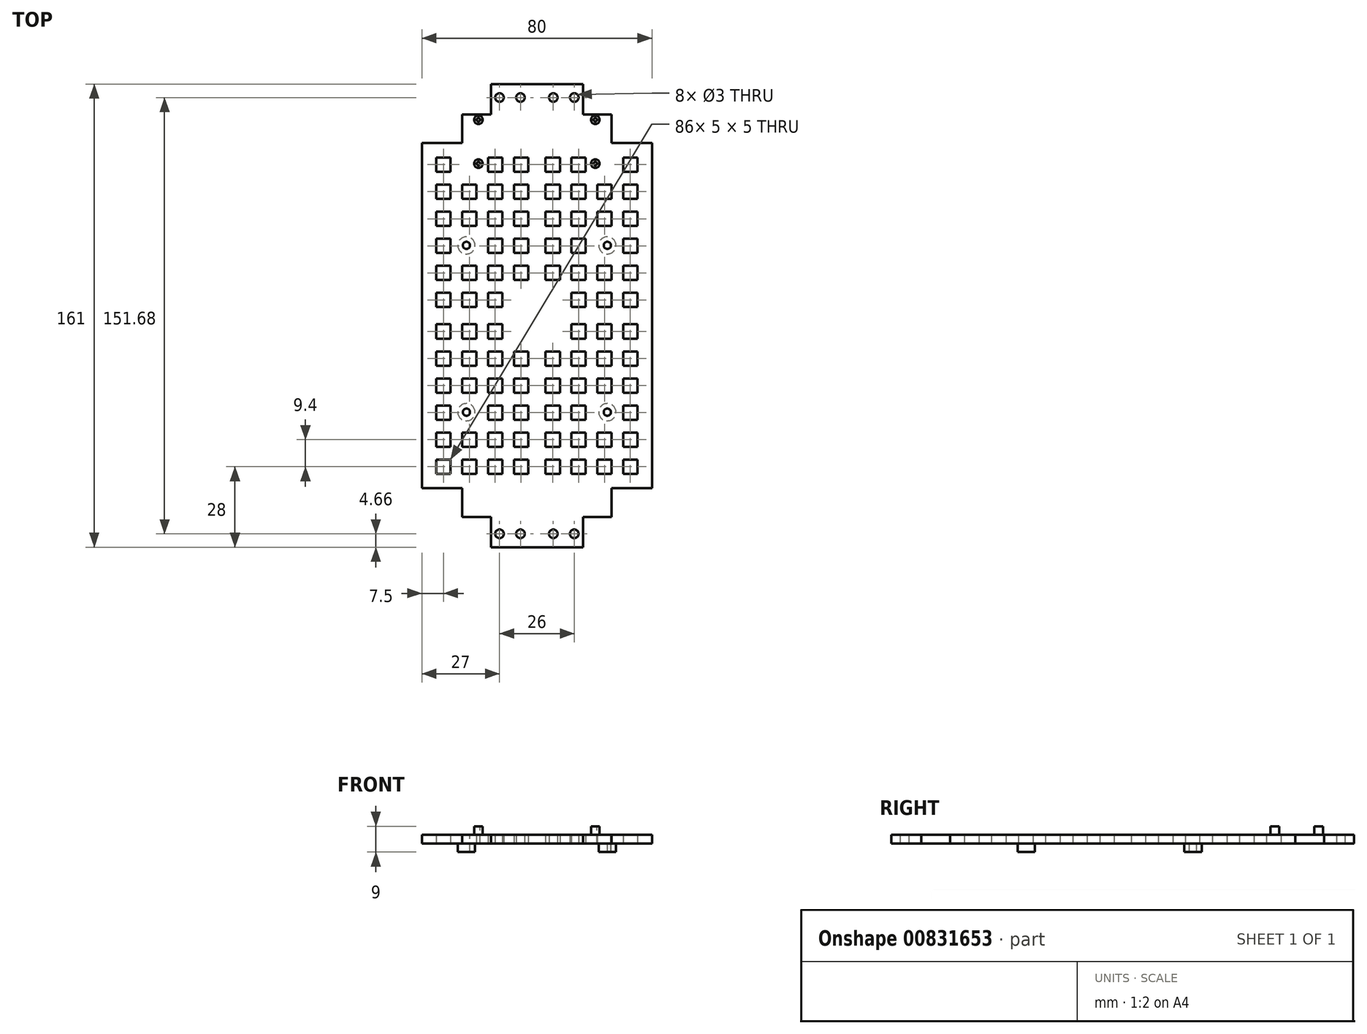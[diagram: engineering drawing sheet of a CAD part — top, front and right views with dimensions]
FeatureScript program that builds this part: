
annotation { "Feature Type Name" : "Feature", "Feature Type Description" : "" }
export const myFeature = defineFeature(function(context is Context, id is Id, definition is map)
    precondition{}
    {
        {
            var Q0;
            Q0=qCreatedBy(makeId("Top.planeOp"),FACE);
            var sketch = newSketch(context, id + "F0", { "sketchPlane" : qUnion([Q0])});
            skLineSegment(sketch, "E0", {"start": v(0, 0) * mm, "end": v(0, 77.06) * mm, "construction": true});
            skLineSegment(sketch, "E1", {"start": v(0, 0) * mm, "end": v(51.76, 0) * mm, "construction": true});
            skLineSegment(sketch, "E2", {"start": v(0, 80.5) * mm, "end": v(16, 80.5) * mm});
            skLineSegment(sketch, "E3", {"start": v(16, 80.5) * mm, "end": v(16, 70) * mm});
            skLineSegment(sketch, "E4", {"start": v(26, 60) * mm, "end": v(40, 60) * mm});
            skLineSegment(sketch, "E5", {"start": v(40, 60) * mm, "end": v(40, 0) * mm});
            skLineSegment(sketch, "E6.MirrorCS", {"start": v(-40, 60) * mm, "end": v(-40, 0) * mm});
            skLineSegment(sketch, "E7.MirrorCS", {"start": v(-26, 60) * mm, "end": v(-40, 60) * mm});
            skLineSegment(sketch, "E8.MirrorCS", {"start": v(0, 80.5) * mm, "end": v(-16, 80.5) * mm});
            skLineSegment(sketch, "E9.MirrorCS", {"start": v(40, -60) * mm, "end": v(40, 0) * mm});
            skLineSegment(sketch, "E10.MirrorCS", {"start": v(-40, -60) * mm, "end": v(-40, 0) * mm});
            skCircle(sketch, "E11", {"center": v(5.7, 75.84) * mm, "radius": 1.5 * mm});
            skCircle(sketch, "E12", {"center": v(13, 75.84) * mm, "radius": 1.5 * mm});
            skLineSegment(sketch, "E13", {"start": v(0, 75.84) * mm, "end": v(16, 75.84) * mm, "construction": true});
            skCircle(sketch, "E14.MirrorC", {"center": v(-13, 75.84) * mm, "radius": 1.5 * mm});
            skCircle(sketch, "E15.MirrorC", {"center": v(-5.7, 75.84) * mm, "radius": 1.5 * mm});
            skLineSegment(sketch, "E16", {"start": v(16, 70) * mm, "end": v(26, 70) * mm});
            skLineSegment(sketch, "E17", {"start": v(26, 70) * mm, "end": v(26, 60) * mm});
            skLineSegment(sketch, "E18.MirrorCS", {"start": v(-26, 70) * mm, "end": v(-26, 60) * mm});
            skLineSegment(sketch, "E19.MirrorCS", {"start": v(-16, 80.5) * mm, "end": v(-16, 70) * mm});
            skLineSegment(sketch, "E20.MirrorCS", {"start": v(-16, 70) * mm, "end": v(-26, 70) * mm});
            skLineSegment(sketch, "E21.MirrorCS", {"start": v(-26, -60) * mm, "end": v(-40, -60) * mm});
            skLineSegment(sketch, "E22.MirrorCS", {"start": v(26, -60) * mm, "end": v(40, -60) * mm});
            skLineSegment(sketch, "E23.MirrorCS", {"start": v(26, -70) * mm, "end": v(26, -60) * mm});
            skLineSegment(sketch, "E24.MirrorCS", {"start": v(16, -70) * mm, "end": v(26, -70) * mm});
            skLineSegment(sketch, "E25.MirrorCS", {"start": v(16, -80.5) * mm, "end": v(16, -70) * mm});
            skLineSegment(sketch, "E26.MirrorCS", {"start": v(0, -80.5) * mm, "end": v(16, -80.5) * mm});
            skLineSegment(sketch, "E27.MirrorCS", {"start": v(0, -80.5) * mm, "end": v(-16, -80.5) * mm});
            skLineSegment(sketch, "E28.MirrorCS", {"start": v(-16, -80.5) * mm, "end": v(-16, -70) * mm});
            skLineSegment(sketch, "E29.MirrorCS", {"start": v(-26, -70) * mm, "end": v(-26, -60) * mm});
            skLineSegment(sketch, "E30.MirrorCS", {"start": v(-16, -70) * mm, "end": v(-26, -70) * mm});
            skCircle(sketch, "E31.MirrorC", {"center": v(13, -75.84) * mm, "radius": 1.5 * mm});
            skCircle(sketch, "E32.MirrorC", {"center": v(5.7, -75.84) * mm, "radius": 1.5 * mm});
            skCircle(sketch, "E33.MirrorC", {"center": v(-13, -75.84) * mm, "radius": 1.5 * mm});
            skCircle(sketch, "E34.MirrorC", {"center": v(-5.7, -75.84) * mm, "radius": 1.5 * mm});
            skLineSegment(sketch, "E35.bottom", {"start": v(35, 50) * mm, "end": v(30, 50) * mm});
            skLineSegment(sketch, "E35.top", {"start": v(35, 55) * mm, "end": v(30, 55) * mm});
            skLineSegment(sketch, "E35.left", {"start": v(35, 50) * mm, "end": v(35, 55) * mm});
            skLineSegment(sketch, "E35.right", {"start": v(30, 50) * mm, "end": v(30, 55) * mm});
            skPoint(sketch, "E35.middle", {"position": v(32.5, 52.5) * mm});
            skPoint(sketch, "E36.1.0.0", {"position": v(23.5, 52.5) * mm});
            skLineSegment(sketch, "E36.1.0.1", {"start": v(26, 55) * mm, "end": v(21, 55) * mm, "construction": true});
            skLineSegment(sketch, "E36.1.0.2", {"start": v(26, 50) * mm, "end": v(21, 50) * mm});
            skLineSegment(sketch, "E36.1.0.3", {"start": v(21, 50) * mm, "end": v(21, 55) * mm, "construction": true});
            skLineSegment(sketch, "E36.1.0.4", {"start": v(26, 50) * mm, "end": v(26, 55) * mm, "construction": true});
            skPoint(sketch, "E36.2.0.0", {"position": v(14.5, 52.5) * mm});
            skLineSegment(sketch, "E36.2.0.1", {"start": v(17, 55) * mm, "end": v(12, 55) * mm});
            skLineSegment(sketch, "E36.2.0.2", {"start": v(17, 50) * mm, "end": v(12, 50) * mm});
            skLineSegment(sketch, "E36.2.0.3", {"start": v(12, 50) * mm, "end": v(12, 55) * mm});
            skLineSegment(sketch, "E36.2.0.4", {"start": v(17, 50) * mm, "end": v(17, 55) * mm});
            skLineSegment(sketch, "E36.direction1", {"start": v(30, 50) * mm, "end": v(21, 50) * mm, "construction": true});
            skPoint(sketch, "E37.0.3.0", {"position": v(5.5, 52.5) * mm});
            skLineSegment(sketch, "E37.1.3.0", {"start": v(8, 55) * mm, "end": v(3, 55) * mm});
            skLineSegment(sketch, "E37.4.3.0", {"start": v(8, 50) * mm, "end": v(3, 50) * mm});
            skLineSegment(sketch, "E37.7.3.0", {"start": v(3, 50) * mm, "end": v(3, 55) * mm});
            skLineSegment(sketch, "E37.10.3.0", {"start": v(8, 50) * mm, "end": v(8, 55) * mm});
            skLineSegment(sketch, "E38.1.0.0", {"start": v(17, 40.6) * mm, "end": v(17, 45.6) * mm});
            skLineSegment(sketch, "E38.1.0.1", {"start": v(3, 40.6) * mm, "end": v(3, 45.6) * mm});
            skLineSegment(sketch, "E38.1.0.2", {"start": v(21, 40.6) * mm, "end": v(21, 45.6) * mm});
            skPoint(sketch, "E38.1.0.3", {"position": v(5.5, 43.1) * mm});
            skLineSegment(sketch, "E38.1.0.4", {"start": v(26, 40.6) * mm, "end": v(26, 45.6) * mm});
            skLineSegment(sketch, "E38.1.0.5", {"start": v(30, 40.6) * mm, "end": v(21, 40.6) * mm, "construction": true});
            skLineSegment(sketch, "E38.1.0.6", {"start": v(35, 45.6) * mm, "end": v(30, 45.6) * mm});
            skLineSegment(sketch, "E38.1.0.7", {"start": v(35, 40.6) * mm, "end": v(35, 45.6) * mm});
            skLineSegment(sketch, "E38.1.0.8", {"start": v(12, 40.6) * mm, "end": v(12, 45.6) * mm});
            skLineSegment(sketch, "E38.1.0.9", {"start": v(17, 40.6) * mm, "end": v(12, 40.6) * mm});
            skPoint(sketch, "E38.1.0.10", {"position": v(23.5, 43.1) * mm});
            skLineSegment(sketch, "E38.1.0.11", {"start": v(8, 40.6) * mm, "end": v(8, 45.6) * mm});
            skLineSegment(sketch, "E38.1.0.12", {"start": v(26, 45.6) * mm, "end": v(21, 45.6) * mm});
            skLineSegment(sketch, "E38.1.0.13", {"start": v(17, 45.6) * mm, "end": v(12, 45.6) * mm});
            skPoint(sketch, "E38.1.0.14", {"position": v(14.5, 43.1) * mm});
            skLineSegment(sketch, "E38.1.0.15", {"start": v(8, 40.6) * mm, "end": v(3, 40.6) * mm});
            skLineSegment(sketch, "E38.1.0.16", {"start": v(35, 40.6) * mm, "end": v(30, 40.6) * mm});
            skPoint(sketch, "E38.1.0.17", {"position": v(32.5, 43.1) * mm});
            skLineSegment(sketch, "E38.1.0.18", {"start": v(8, 45.6) * mm, "end": v(3, 45.6) * mm});
            skLineSegment(sketch, "E38.1.0.19", {"start": v(30, 40.6) * mm, "end": v(30, 45.6) * mm});
            skLineSegment(sketch, "E38.1.0.20", {"start": v(26, 40.6) * mm, "end": v(21, 40.6) * mm});
            skLineSegment(sketch, "E38.2.0.0", {"start": v(17, 31.2) * mm, "end": v(17, 36.2) * mm});
            skLineSegment(sketch, "E38.2.0.1", {"start": v(3, 31.2) * mm, "end": v(3, 36.2) * mm});
            skLineSegment(sketch, "E38.2.0.2", {"start": v(21, 31.2) * mm, "end": v(21, 36.2) * mm});
            skPoint(sketch, "E38.2.0.3", {"position": v(5.5, 33.7) * mm});
            skLineSegment(sketch, "E38.2.0.4", {"start": v(26, 31.2) * mm, "end": v(26, 36.2) * mm});
            skLineSegment(sketch, "E38.2.0.5", {"start": v(30, 31.2) * mm, "end": v(21, 31.2) * mm, "construction": true});
            skLineSegment(sketch, "E38.2.0.6", {"start": v(35, 36.2) * mm, "end": v(30, 36.2) * mm});
            skLineSegment(sketch, "E38.2.0.7", {"start": v(35, 31.2) * mm, "end": v(35, 36.2) * mm});
            skLineSegment(sketch, "E38.2.0.8", {"start": v(12, 31.2) * mm, "end": v(12, 36.2) * mm});
            skLineSegment(sketch, "E38.2.0.9", {"start": v(17, 31.2) * mm, "end": v(12, 31.2) * mm});
            skPoint(sketch, "E38.2.0.10", {"position": v(23.5, 33.7) * mm});
            skLineSegment(sketch, "E38.2.0.11", {"start": v(8, 31.2) * mm, "end": v(8, 36.2) * mm});
            skLineSegment(sketch, "E38.2.0.12", {"start": v(26, 36.2) * mm, "end": v(21, 36.2) * mm});
            skLineSegment(sketch, "E38.2.0.13", {"start": v(17, 36.2) * mm, "end": v(12, 36.2) * mm});
            skPoint(sketch, "E38.2.0.14", {"position": v(14.5, 33.7) * mm});
            skLineSegment(sketch, "E38.2.0.15", {"start": v(8, 31.2) * mm, "end": v(3, 31.2) * mm});
            skLineSegment(sketch, "E38.2.0.16", {"start": v(35, 31.2) * mm, "end": v(30, 31.2) * mm});
            skPoint(sketch, "E38.2.0.17", {"position": v(32.5, 33.7) * mm});
            skLineSegment(sketch, "E38.2.0.18", {"start": v(8, 36.2) * mm, "end": v(3, 36.2) * mm});
            skLineSegment(sketch, "E38.2.0.19", {"start": v(30, 31.2) * mm, "end": v(30, 36.2) * mm});
            skLineSegment(sketch, "E38.2.0.20", {"start": v(26, 31.2) * mm, "end": v(21, 31.2) * mm});
            skLineSegment(sketch, "E38.direction1", {"start": v(3, 50) * mm, "end": v(3, 40.6) * mm, "construction": true});
            skLineSegment(sketch, "E39.0.3.0", {"start": v(17, 21.8) * mm, "end": v(17, 26.8) * mm});
            skLineSegment(sketch, "E39.3.3.0", {"start": v(3, 21.8) * mm, "end": v(3, 26.8) * mm});
            skLineSegment(sketch, "E39.6.3.0", {"start": v(21, 21.8) * mm, "end": v(21, 26.8) * mm, "construction": true});
            skPoint(sketch, "E39.9.3.0", {"position": v(5.5, 24.3) * mm});
            skLineSegment(sketch, "E39.10.3.0", {"start": v(26, 21.8) * mm, "end": v(26, 26.8) * mm, "construction": true});
            skLineSegment(sketch, "E39.13.3.0", {"start": v(30, 21.8) * mm, "end": v(21, 21.8) * mm, "construction": true});
            skLineSegment(sketch, "E39.16.3.0", {"start": v(35, 26.8) * mm, "end": v(30, 26.8) * mm});
            skLineSegment(sketch, "E39.19.3.0", {"start": v(35, 21.8) * mm, "end": v(35, 26.8) * mm});
            skLineSegment(sketch, "E39.22.3.0", {"start": v(12, 21.8) * mm, "end": v(12, 26.8) * mm});
            skLineSegment(sketch, "E39.25.3.0", {"start": v(17, 21.8) * mm, "end": v(12, 21.8) * mm});
            skPoint(sketch, "E39.28.3.0", {"position": v(23.5, 24.3) * mm});
            skLineSegment(sketch, "E39.29.3.0", {"start": v(8, 21.8) * mm, "end": v(8, 26.8) * mm});
            skLineSegment(sketch, "E39.32.3.0", {"start": v(26, 26.8) * mm, "end": v(21, 26.8) * mm, "construction": true});
            skLineSegment(sketch, "E39.35.3.0", {"start": v(17, 26.8) * mm, "end": v(12, 26.8) * mm});
            skPoint(sketch, "E39.38.3.0", {"position": v(14.5, 24.3) * mm});
            skLineSegment(sketch, "E39.39.3.0", {"start": v(8, 21.8) * mm, "end": v(3, 21.8) * mm});
            skLineSegment(sketch, "E39.42.3.0", {"start": v(35, 21.8) * mm, "end": v(30, 21.8) * mm});
            skPoint(sketch, "E39.45.3.0", {"position": v(32.5, 24.3) * mm});
            skLineSegment(sketch, "E39.46.3.0", {"start": v(8, 26.8) * mm, "end": v(3, 26.8) * mm});
            skLineSegment(sketch, "E39.49.3.0", {"start": v(30, 21.8) * mm, "end": v(30, 26.8) * mm});
            skLineSegment(sketch, "E39.52.3.0", {"start": v(26, 21.8) * mm, "end": v(21, 21.8) * mm, "construction": true});
            skLineSegment(sketch, "E39.0.4.0", {"start": v(17, 12.4) * mm, "end": v(17, 17.4) * mm});
            skLineSegment(sketch, "E39.3.4.0", {"start": v(3, 12.4) * mm, "end": v(3, 17.4) * mm});
            skLineSegment(sketch, "E39.6.4.0", {"start": v(21, 12.4) * mm, "end": v(21, 17.4) * mm});
            skPoint(sketch, "E39.9.4.0", {"position": v(5.5, 14.9) * mm});
            skLineSegment(sketch, "E39.10.4.0", {"start": v(26, 12.4) * mm, "end": v(26, 17.4) * mm});
            skLineSegment(sketch, "E39.13.4.0", {"start": v(30, 12.4) * mm, "end": v(21, 12.4) * mm, "construction": true});
            skLineSegment(sketch, "E39.16.4.0", {"start": v(35, 17.4) * mm, "end": v(30, 17.4) * mm});
            skLineSegment(sketch, "E39.19.4.0", {"start": v(35, 12.4) * mm, "end": v(35, 17.4) * mm});
            skLineSegment(sketch, "E39.22.4.0", {"start": v(12, 12.4) * mm, "end": v(12, 17.4) * mm});
            skLineSegment(sketch, "E39.25.4.0", {"start": v(17, 12.4) * mm, "end": v(12, 12.4) * mm});
            skPoint(sketch, "E39.28.4.0", {"position": v(23.5, 14.9) * mm});
            skLineSegment(sketch, "E39.29.4.0", {"start": v(8, 12.4) * mm, "end": v(8, 17.4) * mm});
            skLineSegment(sketch, "E39.32.4.0", {"start": v(26, 17.4) * mm, "end": v(21, 17.4) * mm});
            skLineSegment(sketch, "E39.35.4.0", {"start": v(17, 17.4) * mm, "end": v(12, 17.4) * mm});
            skPoint(sketch, "E39.38.4.0", {"position": v(14.5, 14.9) * mm});
            skLineSegment(sketch, "E39.39.4.0", {"start": v(8, 12.4) * mm, "end": v(3, 12.4) * mm});
            skLineSegment(sketch, "E39.42.4.0", {"start": v(35, 12.4) * mm, "end": v(30, 12.4) * mm});
            skPoint(sketch, "E39.45.4.0", {"position": v(32.5, 14.9) * mm});
            skLineSegment(sketch, "E39.46.4.0", {"start": v(8, 17.4) * mm, "end": v(3, 17.4) * mm});
            skLineSegment(sketch, "E39.49.4.0", {"start": v(30, 12.4) * mm, "end": v(30, 17.4) * mm});
            skLineSegment(sketch, "E39.52.4.0", {"start": v(26, 12.4) * mm, "end": v(21, 12.4) * mm});
            skLineSegment(sketch, "E39.0.5.0", {"start": v(17, 3) * mm, "end": v(17, 8) * mm});
            skLineSegment(sketch, "E39.3.5.0", {"start": v(3, 3) * mm, "end": v(3, 8) * mm, "construction": true});
            skLineSegment(sketch, "E39.6.5.0", {"start": v(21, 3) * mm, "end": v(21, 8) * mm});
            skPoint(sketch, "E39.9.5.0", {"position": v(5.5, 5.5) * mm});
            skLineSegment(sketch, "E39.10.5.0", {"start": v(26, 3) * mm, "end": v(26, 8) * mm});
            skLineSegment(sketch, "E39.13.5.0", {"start": v(30, 3) * mm, "end": v(21, 3) * mm, "construction": true});
            skLineSegment(sketch, "E39.16.5.0", {"start": v(35, 8) * mm, "end": v(30, 8) * mm});
            skLineSegment(sketch, "E39.19.5.0", {"start": v(35, 3) * mm, "end": v(35, 8) * mm});
            skLineSegment(sketch, "E39.22.5.0", {"start": v(12, 3) * mm, "end": v(12, 8) * mm});
            skLineSegment(sketch, "E39.25.5.0", {"start": v(17, 3) * mm, "end": v(12, 3) * mm});
            skPoint(sketch, "E39.28.5.0", {"position": v(23.5, 5.5) * mm});
            skLineSegment(sketch, "E39.29.5.0", {"start": v(8, 3) * mm, "end": v(8, 8) * mm, "construction": true});
            skLineSegment(sketch, "E39.32.5.0", {"start": v(26, 8) * mm, "end": v(21, 8) * mm});
            skLineSegment(sketch, "E39.35.5.0", {"start": v(17, 8) * mm, "end": v(12, 8) * mm});
            skPoint(sketch, "E39.38.5.0", {"position": v(14.5, 5.5) * mm});
            skLineSegment(sketch, "E39.39.5.0", {"start": v(8, 3) * mm, "end": v(3, 3) * mm, "construction": true});
            skLineSegment(sketch, "E39.42.5.0", {"start": v(35, 3) * mm, "end": v(30, 3) * mm});
            skPoint(sketch, "E39.45.5.0", {"position": v(32.5, 5.5) * mm});
            skLineSegment(sketch, "E39.46.5.0", {"start": v(8, 8) * mm, "end": v(3, 8) * mm, "construction": true});
            skLineSegment(sketch, "E39.49.5.0", {"start": v(30, 3) * mm, "end": v(30, 8) * mm});
            skLineSegment(sketch, "E39.52.5.0", {"start": v(26, 3) * mm, "end": v(21, 3) * mm});
            skLineSegment(sketch, "E40.MirrorCS", {"start": v(-26, 3) * mm, "end": v(-21, 3) * mm});
            skLineSegment(sketch, "E41.MirrorCS", {"start": v(-35, 45.6) * mm, "end": v(-30, 45.6) * mm});
            skLineSegment(sketch, "E42.MirrorCS", {"start": v(-26, 12.4) * mm, "end": v(-21, 12.4) * mm});
            skLineSegment(sketch, "E43.MirrorCS", {"start": v(-26, 50) * mm, "end": v(-21, 50) * mm});
            skLineSegment(sketch, "E44.MirrorCS", {"start": v(-26, 21.8) * mm, "end": v(-21, 21.8) * mm, "construction": true});
            skLineSegment(sketch, "E45.MirrorCS", {"start": v(-3, 40.6) * mm, "end": v(-3, 45.6) * mm});
            skLineSegment(sketch, "E46.MirrorCS", {"start": v(-26, 31.2) * mm, "end": v(-21, 31.2) * mm});
            skLineSegment(sketch, "E47.MirrorCS", {"start": v(-26, 40.6) * mm, "end": v(-21, 40.6) * mm});
            skPoint(sketch, "E48.MirrorP", {"position": v(-14.5, 52.5) * mm});
            skPoint(sketch, "E49.MirrorP", {"position": v(-14.5, 14.9) * mm});
            skLineSegment(sketch, "E50.MirrorCS", {"start": v(-30, 3) * mm, "end": v(-21, 3) * mm, "construction": true});
            skLineSegment(sketch, "E51.MirrorCS", {"start": v(-35, 17.4) * mm, "end": v(-30, 17.4) * mm});
            skLineSegment(sketch, "E52.MirrorCS", {"start": v(-8, 40.6) * mm, "end": v(-8, 45.6) * mm});
            skLineSegment(sketch, "E53.MirrorCS", {"start": v(-12, 50) * mm, "end": v(-12, 55) * mm});
            skPoint(sketch, "E54.MirrorP", {"position": v(-23.5, 52.5) * mm});
            skLineSegment(sketch, "E55.MirrorCS", {"start": v(-17, 31.2) * mm, "end": v(-12, 31.2) * mm});
            skPoint(sketch, "E56.MirrorP", {"position": v(-23.5, 14.9) * mm});
            skLineSegment(sketch, "E57.MirrorCS", {"start": v(-35, 21.8) * mm, "end": v(-35, 26.8) * mm});
            skLineSegment(sketch, "E58.MirrorCS", {"start": v(-26, 8) * mm, "end": v(-21, 8) * mm});
            skLineSegment(sketch, "E59.MirrorCS", {"start": v(-8, 36.2) * mm, "end": v(-3, 36.2) * mm});
            skLineSegment(sketch, "E60.MirrorCS", {"start": v(-30, 40.6) * mm, "end": v(-30, 45.6) * mm});
            skPoint(sketch, "E61.MirrorP", {"position": v(-32.5, 43.1) * mm});
            skLineSegment(sketch, "E62.MirrorCS", {"start": v(-17, 17.4) * mm, "end": v(-12, 17.4) * mm});
            skLineSegment(sketch, "E63.MirrorCS", {"start": v(-35, 50) * mm, "end": v(-30, 50) * mm});
            skLineSegment(sketch, "E64.MirrorCS", {"start": v(-8, 50) * mm, "end": v(-8, 55) * mm});
            skPoint(sketch, "E65.MirrorP", {"position": v(-32.5, 5.5) * mm});
            skLineSegment(sketch, "E66.MirrorCS", {"start": v(-17, 26.8) * mm, "end": v(-12, 26.8) * mm});
            skLineSegment(sketch, "E67.MirrorCS", {"start": v(-8, 45.6) * mm, "end": v(-3, 45.6) * mm});
            skLineSegment(sketch, "E68.MirrorCS", {"start": v(-3, 50) * mm, "end": v(-3, 55) * mm});
            skLineSegment(sketch, "E69.MirrorCS", {"start": v(-8, 3) * mm, "end": v(-8, 8) * mm, "construction": true});
            skPoint(sketch, "E70.MirrorP", {"position": v(-14.5, 5.5) * mm});
            skPoint(sketch, "E71.MirrorP", {"position": v(-14.5, 43.1) * mm});
            skLineSegment(sketch, "E72.MirrorCS", {"start": v(-35, 31.2) * mm, "end": v(-30, 31.2) * mm});
            skLineSegment(sketch, "E73.MirrorCS", {"start": v(-26, 17.4) * mm, "end": v(-21, 17.4) * mm});
            skLineSegment(sketch, "E74.MirrorCS", {"start": v(-17, 3) * mm, "end": v(-12, 3) * mm});
            skLineSegment(sketch, "E75.MirrorCS", {"start": v(-26, 26.8) * mm, "end": v(-21, 26.8) * mm, "construction": true});
            skLineSegment(sketch, "E76.MirrorCS", {"start": v(-8, 12.4) * mm, "end": v(-8, 17.4) * mm});
            skLineSegment(sketch, "E77.MirrorCS", {"start": v(-35, 40.6) * mm, "end": v(-30, 40.6) * mm});
            skLineSegment(sketch, "E78.MirrorCS", {"start": v(-8, 50) * mm, "end": v(-3, 50) * mm});
            skLineSegment(sketch, "E79.MirrorCS", {"start": v(-8, 31.2) * mm, "end": v(-3, 31.2) * mm});
            skPoint(sketch, "E80.MirrorP", {"position": v(-23.5, 43.1) * mm});
            skPoint(sketch, "E81.MirrorP", {"position": v(-23.5, 5.5) * mm});
            skLineSegment(sketch, "E82.MirrorCS", {"start": v(-30, 12.4) * mm, "end": v(-21, 12.4) * mm, "construction": true});
            skLineSegment(sketch, "E83.MirrorCS", {"start": v(-35, 26.8) * mm, "end": v(-30, 26.8) * mm});
            skLineSegment(sketch, "E84.MirrorCS", {"start": v(-17, 40.6) * mm, "end": v(-12, 40.6) * mm});
            skLineSegment(sketch, "E85.MirrorCS", {"start": v(-12, 31.2) * mm, "end": v(-12, 36.2) * mm});
            skLineSegment(sketch, "E86.MirrorCS", {"start": v(-26, 3) * mm, "end": v(-26, 8) * mm});
            skLineSegment(sketch, "E87.MirrorCS", {"start": v(-17, 50) * mm, "end": v(-12, 50) * mm});
            skPoint(sketch, "E88.MirrorP", {"position": v(-5.5, 14.9) * mm});
            skPoint(sketch, "E89.MirrorP", {"position": v(-32.5, 52.5) * mm});
            skPoint(sketch, "E90.MirrorP", {"position": v(-32.5, 24.3) * mm});
            skPoint(sketch, "E91.MirrorP", {"position": v(-14.5, 24.3) * mm});
            skLineSegment(sketch, "E92.MirrorCS", {"start": v(-35, 31.2) * mm, "end": v(-35, 36.2) * mm});
            skLineSegment(sketch, "E93.MirrorCS", {"start": v(-26, 12.4) * mm, "end": v(-26, 17.4) * mm});
            skLineSegment(sketch, "E94.MirrorCS", {"start": v(-30, 21.8) * mm, "end": v(-21, 21.8) * mm, "construction": true});
            skLineSegment(sketch, "E95.MirrorCS", {"start": v(-17, 55) * mm, "end": v(-12, 55) * mm});
            skLineSegment(sketch, "E96.MirrorCS", {"start": v(-21, 3) * mm, "end": v(-21, 8) * mm});
            skLineSegment(sketch, "E97.MirrorCS", {"start": v(-3, 3) * mm, "end": v(-3, 8) * mm, "construction": true});
            skLineSegment(sketch, "E98.MirrorCS", {"start": v(-35, 36.2) * mm, "end": v(-30, 36.2) * mm});
            skLineSegment(sketch, "E99.MirrorCS", {"start": v(-35, 40.6) * mm, "end": v(-35, 45.6) * mm});
            skLineSegment(sketch, "E100.MirrorCS", {"start": v(-26, 50) * mm, "end": v(-26, 55) * mm, "construction": true});
            skLineSegment(sketch, "E101.MirrorCS", {"start": v(-12, 40.6) * mm, "end": v(-12, 45.6) * mm});
            skLineSegment(sketch, "E102.MirrorCS", {"start": v(-26, 21.8) * mm, "end": v(-26, 26.8) * mm, "construction": true});
            skLineSegment(sketch, "E103.MirrorCS", {"start": v(-21, 12.4) * mm, "end": v(-21, 17.4) * mm});
            skLineSegment(sketch, "E104.MirrorCS", {"start": v(-8, 55) * mm, "end": v(-3, 55) * mm});
            skLineSegment(sketch, "E105.MirrorCS", {"start": v(-30, 31.2) * mm, "end": v(-21, 31.2) * mm, "construction": true});
            skLineSegment(sketch, "E106.MirrorCS", {"start": v(-17, 3) * mm, "end": v(-17, 8) * mm});
            skLineSegment(sketch, "E107.MirrorCS", {"start": v(-3, 12.4) * mm, "end": v(-3, 17.4) * mm});
            skLineSegment(sketch, "E108.MirrorCS", {"start": v(-21, 21.8) * mm, "end": v(-21, 26.8) * mm, "construction": true});
            skLineSegment(sketch, "E109.MirrorCS", {"start": v(-8, 40.6) * mm, "end": v(-3, 40.6) * mm});
            skPoint(sketch, "E110.MirrorP", {"position": v(-5.5, 5.5) * mm});
            skPoint(sketch, "E111.MirrorP", {"position": v(-5.5, 43.1) * mm});
            skLineSegment(sketch, "E112.MirrorCS", {"start": v(-17, 36.2) * mm, "end": v(-12, 36.2) * mm});
            skLineSegment(sketch, "E113.MirrorCS", {"start": v(-21, 50) * mm, "end": v(-21, 55) * mm, "construction": true});
            skPoint(sketch, "E114.MirrorP", {"position": v(-23.5, 24.3) * mm});
            skPoint(sketch, "E115.MirrorP", {"position": v(-5.5, 24.3) * mm});
            skLineSegment(sketch, "E116.MirrorCS", {"start": v(-17, 12.4) * mm, "end": v(-12, 12.4) * mm});
            skLineSegment(sketch, "E117.MirrorCS", {"start": v(-8, 21.8) * mm, "end": v(-8, 26.8) * mm});
            skLineSegment(sketch, "E118.MirrorCS", {"start": v(-30, 40.6) * mm, "end": v(-21, 40.6) * mm, "construction": true});
            skLineSegment(sketch, "E119.MirrorCS", {"start": v(-30, 3) * mm, "end": v(-30, 8) * mm});
            skLineSegment(sketch, "E120.MirrorCS", {"start": v(-17, 12.4) * mm, "end": v(-17, 17.4) * mm});
            skLineSegment(sketch, "E121.MirrorCS", {"start": v(-26, 31.2) * mm, "end": v(-26, 36.2) * mm});
            skLineSegment(sketch, "E122.MirrorCS", {"start": v(-26, 55) * mm, "end": v(-21, 55) * mm, "construction": true});
            skLineSegment(sketch, "E123.MirrorCS", {"start": v(-3, 21.8) * mm, "end": v(-3, 26.8) * mm});
            skLineSegment(sketch, "E124.MirrorCS", {"start": v(-8, 8) * mm, "end": v(-3, 8) * mm, "construction": true});
            skLineSegment(sketch, "E125.MirrorCS", {"start": v(-12, 3) * mm, "end": v(-12, 8) * mm});
            skLineSegment(sketch, "E126.MirrorCS", {"start": v(-30, 12.4) * mm, "end": v(-30, 17.4) * mm});
            skLineSegment(sketch, "E127.MirrorCS", {"start": v(-17, 21.8) * mm, "end": v(-17, 26.8) * mm});
            skLineSegment(sketch, "E128.MirrorCS", {"start": v(-8, 17.4) * mm, "end": v(-3, 17.4) * mm});
            skLineSegment(sketch, "E129.MirrorCS", {"start": v(-30, 50) * mm, "end": v(-21, 50) * mm, "construction": true});
            skLineSegment(sketch, "E130.MirrorCS", {"start": v(-3, 50) * mm, "end": v(-3, 40.6) * mm, "construction": true});
            skLineSegment(sketch, "E131.MirrorCS", {"start": v(-21, 40.6) * mm, "end": v(-21, 45.6) * mm});
            skLineSegment(sketch, "E132.MirrorCS", {"start": v(-30, 50) * mm, "end": v(-30, 55) * mm});
            skLineSegment(sketch, "E133.MirrorCS", {"start": v(-21, 31.2) * mm, "end": v(-21, 36.2) * mm});
            skLineSegment(sketch, "E134.MirrorCS", {"start": v(-30, 21.8) * mm, "end": v(-30, 26.8) * mm});
            skLineSegment(sketch, "E135.MirrorCS", {"start": v(-3, 31.2) * mm, "end": v(-3, 36.2) * mm});
            skLineSegment(sketch, "E136.MirrorCS", {"start": v(-35, 3) * mm, "end": v(-30, 3) * mm});
            skLineSegment(sketch, "E137.MirrorCS", {"start": v(-26, 40.6) * mm, "end": v(-26, 45.6) * mm});
            skPoint(sketch, "E138.MirrorP", {"position": v(-32.5, 33.7) * mm});
            skLineSegment(sketch, "E139.MirrorCS", {"start": v(-35, 3) * mm, "end": v(-35, 8) * mm});
            skLineSegment(sketch, "E140.MirrorCS", {"start": v(-12, 12.4) * mm, "end": v(-12, 17.4) * mm});
            skLineSegment(sketch, "E141.MirrorCS", {"start": v(-17, 21.8) * mm, "end": v(-12, 21.8) * mm});
            skPoint(sketch, "E142.MirrorP", {"position": v(-14.5, 33.7) * mm});
            skLineSegment(sketch, "E143.MirrorCS", {"start": v(-8, 3) * mm, "end": v(-3, 3) * mm, "construction": true});
            skLineSegment(sketch, "E144.MirrorCS", {"start": v(-17, 31.2) * mm, "end": v(-17, 36.2) * mm});
            skLineSegment(sketch, "E145.MirrorCS", {"start": v(-35, 12.4) * mm, "end": v(-30, 12.4) * mm});
            skLineSegment(sketch, "E146.MirrorCS", {"start": v(-35, 50) * mm, "end": v(-35, 55) * mm});
            skLineSegment(sketch, "E147.MirrorCS", {"start": v(-8, 26.8) * mm, "end": v(-3, 26.8) * mm});
            skLineSegment(sketch, "E148.MirrorCS", {"start": v(-17, 45.6) * mm, "end": v(-12, 45.6) * mm});
            skLineSegment(sketch, "E149.MirrorCS", {"start": v(-26, 36.2) * mm, "end": v(-21, 36.2) * mm});
            skLineSegment(sketch, "E150.MirrorCS", {"start": v(-8, 21.8) * mm, "end": v(-3, 21.8) * mm});
            skPoint(sketch, "E151.MirrorP", {"position": v(-5.5, 52.5) * mm});
            skPoint(sketch, "E152.MirrorP", {"position": v(-32.5, 14.9) * mm});
            skPoint(sketch, "E153.MirrorP", {"position": v(-23.5, 33.7) * mm});
            skLineSegment(sketch, "E154.MirrorCS", {"start": v(-17, 8) * mm, "end": v(-12, 8) * mm});
            skLineSegment(sketch, "E155.MirrorCS", {"start": v(-17, 40.6) * mm, "end": v(-17, 45.6) * mm});
            skLineSegment(sketch, "E156.MirrorCS", {"start": v(-35, 55) * mm, "end": v(-30, 55) * mm});
            skPoint(sketch, "E157.MirrorP", {"position": v(-5.5, 33.7) * mm});
            skLineSegment(sketch, "E158.MirrorCS", {"start": v(-8, 12.4) * mm, "end": v(-3, 12.4) * mm});
            skLineSegment(sketch, "E159.MirrorCS", {"start": v(-35, 21.8) * mm, "end": v(-30, 21.8) * mm});
            skLineSegment(sketch, "E160.MirrorCS", {"start": v(-30, 31.2) * mm, "end": v(-30, 36.2) * mm});
            skLineSegment(sketch, "E161.MirrorCS", {"start": v(-35, 12.4) * mm, "end": v(-35, 17.4) * mm});
            skLineSegment(sketch, "E162.MirrorCS", {"start": v(-35, 8) * mm, "end": v(-30, 8) * mm});
            skLineSegment(sketch, "E163.MirrorCS", {"start": v(-17, 50) * mm, "end": v(-17, 55) * mm});
            skLineSegment(sketch, "E164.MirrorCS", {"start": v(-12, 21.8) * mm, "end": v(-12, 26.8) * mm});
            skLineSegment(sketch, "E165.MirrorCS", {"start": v(-26, 45.6) * mm, "end": v(-21, 45.6) * mm});
            skLineSegment(sketch, "E166.MirrorCS", {"start": v(-8, 31.2) * mm, "end": v(-8, 36.2) * mm});
            skLineSegment(sketch, "E167.MirrorCS", {"start": v(-26, -31.2) * mm, "end": v(-21, -31.2) * mm, "construction": true});
            skLineSegment(sketch, "E168.MirrorCS", {"start": v(-26, -50) * mm, "end": v(-21, -50) * mm});
            skLineSegment(sketch, "E169.MirrorCS", {"start": v(-26, -40.6) * mm, "end": v(-21, -40.6) * mm});
            skLineSegment(sketch, "E170.MirrorCS", {"start": v(26, -40.6) * mm, "end": v(21, -40.6) * mm});
            skLineSegment(sketch, "E171.MirrorCS", {"start": v(26, -31.2) * mm, "end": v(21, -31.2) * mm, "construction": true});
            skLineSegment(sketch, "E172.MirrorCS", {"start": v(3, -40.6) * mm, "end": v(3, -45.6) * mm});
            skLineSegment(sketch, "E173.MirrorCS", {"start": v(26, -50) * mm, "end": v(21, -50) * mm});
            skLineSegment(sketch, "E174.MirrorCS", {"start": v(26, -12.4) * mm, "end": v(21, -12.4) * mm});
            skLineSegment(sketch, "E175.MirrorCS", {"start": v(26, -21.8) * mm, "end": v(21, -21.8) * mm});
            skLineSegment(sketch, "E176.MirrorCS", {"start": v(35, -45.6) * mm, "end": v(30, -45.6) * mm});
            skLineSegment(sketch, "E177.MirrorCS", {"start": v(-26, -3) * mm, "end": v(-21, -3) * mm});
            skLineSegment(sketch, "E178.MirrorCS", {"start": v(-26, -21.8) * mm, "end": v(-21, -21.8) * mm});
            skLineSegment(sketch, "E179.MirrorCS", {"start": v(26, -3) * mm, "end": v(21, -3) * mm});
            skLineSegment(sketch, "E180.MirrorCS", {"start": v(-3, -40.6) * mm, "end": v(-3, -45.6) * mm});
            skLineSegment(sketch, "E181.MirrorCS", {"start": v(-26, -12.4) * mm, "end": v(-21, -12.4) * mm});
            skLineSegment(sketch, "E182.MirrorCS", {"start": v(30, -31.2) * mm, "end": v(21, -31.2) * mm, "construction": true});
            skPoint(sketch, "E183.MirrorP", {"position": v(-23.5, -5.5) * mm});
            skLineSegment(sketch, "E184.MirrorCS", {"start": v(26, -36.2) * mm, "end": v(21, -36.2) * mm, "construction": true});
            skPoint(sketch, "E185.MirrorP", {"position": v(-23.5, -43.1) * mm});
            skLineSegment(sketch, "E186.MirrorCS", {"start": v(-26, -31.2) * mm, "end": v(-26, -36.2) * mm, "construction": true});
            skPoint(sketch, "E187.MirrorP", {"position": v(23.5, -5.5) * mm});
            skLineSegment(sketch, "E188.MirrorCS", {"start": v(17, -21.8) * mm, "end": v(12, -21.8) * mm});
            skLineSegment(sketch, "E189.MirrorCS", {"start": v(26, -12.4) * mm, "end": v(26, -17.4) * mm});
            skLineSegment(sketch, "E190.MirrorCS", {"start": v(-21, -12.4) * mm, "end": v(-21, -17.4) * mm});
            skPoint(sketch, "E191.MirrorP", {"position": v(23.5, -14.9) * mm});
            skLineSegment(sketch, "E192.MirrorCS", {"start": v(30, -21.8) * mm, "end": v(21, -21.8) * mm, "construction": true});
            skLineSegment(sketch, "E193.MirrorCS", {"start": v(-35, -12.4) * mm, "end": v(-35, -17.4) * mm});
            skLineSegment(sketch, "E194.MirrorCS", {"start": v(-35, -45.6) * mm, "end": v(-30, -45.6) * mm});
            skLineSegment(sketch, "E195.MirrorCS", {"start": v(-3, -50) * mm, "end": v(-3, -55) * mm});
            skLineSegment(sketch, "E196.MirrorCS", {"start": v(-8, -17.4) * mm, "end": v(-3, -17.4) * mm});
            skLineSegment(sketch, "E197.MirrorCS", {"start": v(-21, -21.8) * mm, "end": v(-21, -26.8) * mm});
            skLineSegment(sketch, "E198.MirrorCS", {"start": v(-35, -31.2) * mm, "end": v(-35, -36.2) * mm});
            skLineSegment(sketch, "E199.MirrorCS", {"start": v(8, -21.8) * mm, "end": v(8, -26.8) * mm});
            skLineSegment(sketch, "E200.MirrorCS", {"start": v(17, -12.4) * mm, "end": v(12, -12.4) * mm});
            skPoint(sketch, "E201.MirrorP", {"position": v(-5.5, -5.5) * mm});
            skLineSegment(sketch, "E202.MirrorCS", {"start": v(17, -50) * mm, "end": v(12, -50) * mm});
            skPoint(sketch, "E203.MirrorP", {"position": v(14.5, -5.5) * mm});
            skLineSegment(sketch, "E204.MirrorCS", {"start": v(17, -40.6) * mm, "end": v(12, -40.6) * mm});
            skLineSegment(sketch, "E205.MirrorCS", {"start": v(17, -55) * mm, "end": v(12, -55) * mm});
            skLineSegment(sketch, "E206.MirrorCS", {"start": v(-8, -31.2) * mm, "end": v(-8, -36.2) * mm});
            skPoint(sketch, "E207.MirrorP", {"position": v(-5.5, -14.9) * mm});
            skLineSegment(sketch, "E208.MirrorCS", {"start": v(30, -12.4) * mm, "end": v(21, -12.4) * mm, "construction": true});
            skLineSegment(sketch, "E209.MirrorCS", {"start": v(26, -3) * mm, "end": v(26, -8) * mm});
            skLineSegment(sketch, "E210.MirrorCS", {"start": v(12, -3) * mm, "end": v(12, -8) * mm});
            skLineSegment(sketch, "E211.MirrorCS", {"start": v(-12, -3) * mm, "end": v(-12, -8) * mm});
            skLineSegment(sketch, "E212.MirrorCS", {"start": v(-17, -21.8) * mm, "end": v(-12, -21.8) * mm});
            skLineSegment(sketch, "E213.MirrorCS", {"start": v(-17, -45.6) * mm, "end": v(-12, -45.6) * mm});
            skLineSegment(sketch, "E214.MirrorCS", {"start": v(-8, -3) * mm, "end": v(-3, -3) * mm, "construction": true});
            skLineSegment(sketch, "E215.MirrorCS", {"start": v(-12, -31.2) * mm, "end": v(-12, -36.2) * mm});
            skLineSegment(sketch, "E216.MirrorCS", {"start": v(-17, -50) * mm, "end": v(-17, -55) * mm});
            skLineSegment(sketch, "E217.MirrorCS", {"start": v(-8, -50) * mm, "end": v(-8, -55) * mm});
            skLineSegment(sketch, "E218.MirrorCS", {"start": v(-30, -31.2) * mm, "end": v(-21, -31.2) * mm, "construction": true});
            skPoint(sketch, "E219.MirrorP", {"position": v(32.5, -14.9) * mm});
            skLineSegment(sketch, "E220.MirrorCS", {"start": v(35, -17.4) * mm, "end": v(30, -17.4) * mm});
            skPoint(sketch, "E221.MirrorP", {"position": v(-32.5, -52.5) * mm});
            skLineSegment(sketch, "E222.MirrorCS", {"start": v(35, -21.8) * mm, "end": v(35, -26.8) * mm});
            skLineSegment(sketch, "E223.MirrorCS", {"start": v(30, -3) * mm, "end": v(21, -3) * mm, "construction": true});
            skLineSegment(sketch, "E224.MirrorCS", {"start": v(12, -50) * mm, "end": v(12, -55) * mm});
            skPoint(sketch, "E225.MirrorP", {"position": v(5.5, -52.5) * mm});
            skLineSegment(sketch, "E226.MirrorCS", {"start": v(8, -40.6) * mm, "end": v(8, -45.6) * mm});
            skLineSegment(sketch, "E227.MirrorCS", {"start": v(17, -31.2) * mm, "end": v(12, -31.2) * mm});
            skLineSegment(sketch, "E228.MirrorCS", {"start": v(8, -12.4) * mm, "end": v(8, -17.4) * mm});
            skLineSegment(sketch, "E229.MirrorCS", {"start": v(17, -3) * mm, "end": v(12, -3) * mm});
            skLineSegment(sketch, "E230.MirrorCS", {"start": v(8, -50) * mm, "end": v(3, -50) * mm});
            skPoint(sketch, "E231.MirrorP", {"position": v(32.5, -5.5) * mm});
            skLineSegment(sketch, "E232.MirrorCS", {"start": v(26, -26.8) * mm, "end": v(21, -26.8) * mm});
            skPoint(sketch, "E233.MirrorP", {"position": v(-5.5, -43.1) * mm});
            skPoint(sketch, "E234.MirrorP", {"position": v(32.5, -43.1) * mm});
            skLineSegment(sketch, "E235.MirrorCS", {"start": v(35, -40.6) * mm, "end": v(30, -40.6) * mm});
            skLineSegment(sketch, "E236.MirrorCS", {"start": v(8, -31.2) * mm, "end": v(3, -31.2) * mm});
            skLineSegment(sketch, "E237.MirrorCS", {"start": v(-17, -26.8) * mm, "end": v(-12, -26.8) * mm});
            skLineSegment(sketch, "E238.MirrorCS", {"start": v(-8, -3) * mm, "end": v(-8, -8) * mm, "construction": true});
            skLineSegment(sketch, "E239.MirrorCS", {"start": v(-8, -26.8) * mm, "end": v(-3, -26.8) * mm});
            skLineSegment(sketch, "E240.MirrorCS", {"start": v(-8, -40.6) * mm, "end": v(-3, -40.6) * mm});
            skLineSegment(sketch, "E241.MirrorCS", {"start": v(-26, -12.4) * mm, "end": v(-26, -17.4) * mm});
            skLineSegment(sketch, "E242.MirrorCS", {"start": v(-30, -50) * mm, "end": v(-21, -50) * mm, "construction": true});
            skLineSegment(sketch, "E243.MirrorCS", {"start": v(26, -21.8) * mm, "end": v(26, -26.8) * mm});
            skLineSegment(sketch, "E244.MirrorCS", {"start": v(8, -55) * mm, "end": v(3, -55) * mm});
            skLineSegment(sketch, "E245.MirrorCS", {"start": v(8, -40.6) * mm, "end": v(3, -40.6) * mm});
            skPoint(sketch, "E246.MirrorP", {"position": v(14.5, -43.1) * mm});
            skLineSegment(sketch, "E247.MirrorCS", {"start": v(-17, -17.4) * mm, "end": v(-12, -17.4) * mm});
            skLineSegment(sketch, "E248.MirrorCS", {"start": v(35, -31.2) * mm, "end": v(30, -31.2) * mm});
            skLineSegment(sketch, "E249.MirrorCS", {"start": v(3, -50) * mm, "end": v(3, -55) * mm});
            skLineSegment(sketch, "E250.MirrorCS", {"start": v(8, -45.6) * mm, "end": v(3, -45.6) * mm});
            skPoint(sketch, "E251.MirrorP", {"position": v(5.5, -33.7) * mm});
            skLineSegment(sketch, "E252.MirrorCS", {"start": v(26, -17.4) * mm, "end": v(21, -17.4) * mm});
            skLineSegment(sketch, "E253.MirrorCS", {"start": v(-30, -3) * mm, "end": v(-21, -3) * mm, "construction": true});
            skLineSegment(sketch, "E254.MirrorCS", {"start": v(-30, -21.8) * mm, "end": v(-21, -21.8) * mm, "construction": true});
            skLineSegment(sketch, "E255.MirrorCS", {"start": v(17, -26.8) * mm, "end": v(12, -26.8) * mm});
            skLineSegment(sketch, "E256.MirrorCS", {"start": v(-17, -36.2) * mm, "end": v(-12, -36.2) * mm});
            skLineSegment(sketch, "E257.MirrorCS", {"start": v(8, -3) * mm, "end": v(8, -8) * mm, "construction": true});
            skLineSegment(sketch, "E258.MirrorCS", {"start": v(-35, -31.2) * mm, "end": v(-30, -31.2) * mm});
            skLineSegment(sketch, "E259.MirrorCS", {"start": v(-3, -50) * mm, "end": v(-3, -40.6) * mm, "construction": true});
            skPoint(sketch, "E260.MirrorP", {"position": v(-14.5, -52.5) * mm});
            skPoint(sketch, "E261.MirrorP", {"position": v(-23.5, -24.3) * mm});
            skPoint(sketch, "E262.MirrorP", {"position": v(-5.5, -24.3) * mm});
            skLineSegment(sketch, "E263.MirrorCS", {"start": v(26, -8) * mm, "end": v(21, -8) * mm});
            skLineSegment(sketch, "E264.MirrorCS", {"start": v(17, -17.4) * mm, "end": v(12, -17.4) * mm});
            skPoint(sketch, "E265.MirrorP", {"position": v(-14.5, -14.9) * mm});
            skLineSegment(sketch, "E266.MirrorCS", {"start": v(-21, -40.6) * mm, "end": v(-21, -45.6) * mm});
            skLineSegment(sketch, "E267.MirrorCS", {"start": v(8, -21.8) * mm, "end": v(3, -21.8) * mm});
            skLineSegment(sketch, "E268.MirrorCS", {"start": v(8, -36.2) * mm, "end": v(3, -36.2) * mm});
            skLineSegment(sketch, "E269.MirrorCS", {"start": v(30, -40.6) * mm, "end": v(30, -45.6) * mm});
            skPoint(sketch, "E270.MirrorP", {"position": v(14.5, -33.7) * mm});
            skLineSegment(sketch, "E271.MirrorCS", {"start": v(30, -31.2) * mm, "end": v(30, -36.2) * mm});
            skPoint(sketch, "E272.MirrorP", {"position": v(23.5, -33.7) * mm});
            skLineSegment(sketch, "E273.MirrorCS", {"start": v(17, -36.2) * mm, "end": v(12, -36.2) * mm});
            skLineSegment(sketch, "E274.MirrorCS", {"start": v(-35, -17.4) * mm, "end": v(-30, -17.4) * mm});
            skLineSegment(sketch, "E275.MirrorCS", {"start": v(-12, -12.4) * mm, "end": v(-12, -17.4) * mm});
            skLineSegment(sketch, "E276.MirrorCS", {"start": v(8, -50) * mm, "end": v(8, -55) * mm});
            skLineSegment(sketch, "E277.MirrorCS", {"start": v(35, -50) * mm, "end": v(30, -50) * mm});
            skLineSegment(sketch, "E278.MirrorCS", {"start": v(35, -55) * mm, "end": v(30, -55) * mm});
            skLineSegment(sketch, "E279.MirrorCS", {"start": v(17, -40.6) * mm, "end": v(17, -45.6) * mm});
            skLineSegment(sketch, "E280.MirrorCS", {"start": v(8, -12.4) * mm, "end": v(3, -12.4) * mm});
            skLineSegment(sketch, "E281.MirrorCS", {"start": v(-8, -40.6) * mm, "end": v(-8, -45.6) * mm});
            skLineSegment(sketch, "E282.MirrorCS", {"start": v(17, -8) * mm, "end": v(12, -8) * mm});
            skLineSegment(sketch, "E283.MirrorCS", {"start": v(-30, -50) * mm, "end": v(-30, -55) * mm});
            skPoint(sketch, "E284.MirrorP", {"position": v(-32.5, -33.7) * mm});
            skLineSegment(sketch, "E285.MirrorCS", {"start": v(-21, -3) * mm, "end": v(-21, -8) * mm});
            skLineSegment(sketch, "E286.MirrorCS", {"start": v(-26, -17.4) * mm, "end": v(-21, -17.4) * mm});
            skLineSegment(sketch, "E287.MirrorCS", {"start": v(-17, -55) * mm, "end": v(-12, -55) * mm});
            skLineSegment(sketch, "E288.MirrorCS", {"start": v(-21, -50) * mm, "end": v(-21, -55) * mm});
            skPoint(sketch, "E289.MirrorP", {"position": v(-23.5, -52.5) * mm});
            skLineSegment(sketch, "E290.MirrorCS", {"start": v(35, -21.8) * mm, "end": v(30, -21.8) * mm});
            skLineSegment(sketch, "E291.MirrorCS", {"start": v(-8, -21.8) * mm, "end": v(-3, -21.8) * mm});
            skLineSegment(sketch, "E292.MirrorCS", {"start": v(-17, -3) * mm, "end": v(-12, -3) * mm});
            skLineSegment(sketch, "E293.MirrorCS", {"start": v(-17, -12.4) * mm, "end": v(-12, -12.4) * mm});
            skLineSegment(sketch, "E294.MirrorCS", {"start": v(-26, -36.2) * mm, "end": v(-21, -36.2) * mm, "construction": true});
            skPoint(sketch, "E295.MirrorP", {"position": v(32.5, -33.7) * mm});
            skLineSegment(sketch, "E296.MirrorCS", {"start": v(35, -50) * mm, "end": v(35, -55) * mm});
            skLineSegment(sketch, "E297.MirrorCS", {"start": v(8, -26.8) * mm, "end": v(3, -26.8) * mm});
            skLineSegment(sketch, "E298.MirrorCS", {"start": v(35, -12.4) * mm, "end": v(30, -12.4) * mm});
            skLineSegment(sketch, "E299.MirrorCS", {"start": v(-12, -50) * mm, "end": v(-12, -55) * mm});
            skLineSegment(sketch, "E300.MirrorCS", {"start": v(-17, -8) * mm, "end": v(-12, -8) * mm});
            skLineSegment(sketch, "E301.MirrorCS", {"start": v(-26, -26.8) * mm, "end": v(-21, -26.8) * mm});
            skLineSegment(sketch, "E302.MirrorCS", {"start": v(30, -21.8) * mm, "end": v(30, -26.8) * mm});
            skLineSegment(sketch, "E303.MirrorCS", {"start": v(30, -50) * mm, "end": v(30, -55) * mm});
            skPoint(sketch, "E304.MirrorP", {"position": v(-5.5, -52.5) * mm});
            skPoint(sketch, "E305.MirrorP", {"position": v(-23.5, -14.9) * mm});
            skLineSegment(sketch, "E306.MirrorCS", {"start": v(17, -31.2) * mm, "end": v(17, -36.2) * mm});
            skPoint(sketch, "E307.MirrorP", {"position": v(-14.5, -33.7) * mm});
            skLineSegment(sketch, "E308.MirrorCS", {"start": v(8, -3) * mm, "end": v(3, -3) * mm, "construction": true});
            skLineSegment(sketch, "E309.MirrorCS", {"start": v(-8, -21.8) * mm, "end": v(-8, -26.8) * mm});
            skLineSegment(sketch, "E310.MirrorCS", {"start": v(-3, -3) * mm, "end": v(-3, -8) * mm, "construction": true});
            skLineSegment(sketch, "E311.MirrorCS", {"start": v(8, -17.4) * mm, "end": v(3, -17.4) * mm});
            skLineSegment(sketch, "E312.MirrorCS", {"start": v(-21, -31.2) * mm, "end": v(-21, -36.2) * mm, "construction": true});
            skLineSegment(sketch, "E313.MirrorCS", {"start": v(-17, -31.2) * mm, "end": v(-12, -31.2) * mm});
            skLineSegment(sketch, "E314.MirrorCS", {"start": v(35, -3) * mm, "end": v(30, -3) * mm});
            skLineSegment(sketch, "E315.MirrorCS", {"start": v(-35, -36.2) * mm, "end": v(-30, -36.2) * mm});
            skLineSegment(sketch, "E316.MirrorCS", {"start": v(-30, -21.8) * mm, "end": v(-30, -26.8) * mm});
            skLineSegment(sketch, "E317.MirrorCS", {"start": v(-30, -40.6) * mm, "end": v(-21, -40.6) * mm, "construction": true});
            skPoint(sketch, "E318.MirrorP", {"position": v(-32.5, -43.1) * mm});
            skLineSegment(sketch, "E319.MirrorCS", {"start": v(-17, -40.6) * mm, "end": v(-17, -45.6) * mm});
            skLineSegment(sketch, "E320.MirrorCS", {"start": v(-8, -12.4) * mm, "end": v(-8, -17.4) * mm});
            skLineSegment(sketch, "E321.MirrorCS", {"start": v(3, -50) * mm, "end": v(3, -40.6) * mm, "construction": true});
            skLineSegment(sketch, "E322.MirrorCS", {"start": v(21, -40.6) * mm, "end": v(21, -45.6) * mm});
            skLineSegment(sketch, "E323.MirrorCS", {"start": v(3, -31.2) * mm, "end": v(3, -36.2) * mm});
            skPoint(sketch, "E324.MirrorP", {"position": v(5.5, -24.3) * mm});
            skLineSegment(sketch, "E325.MirrorCS", {"start": v(30, -40.6) * mm, "end": v(21, -40.6) * mm, "construction": true});
            skPoint(sketch, "E326.MirrorP", {"position": v(-23.5, -33.7) * mm});
            skLineSegment(sketch, "E327.MirrorCS", {"start": v(26, -31.2) * mm, "end": v(26, -36.2) * mm, "construction": true});
            skPoint(sketch, "E328.MirrorP", {"position": v(-14.5, -5.5) * mm});
            skLineSegment(sketch, "E329.MirrorCS", {"start": v(3, -21.8) * mm, "end": v(3, -26.8) * mm});
            skLineSegment(sketch, "E330.MirrorCS", {"start": v(17, -12.4) * mm, "end": v(17, -17.4) * mm});
            skLineSegment(sketch, "E331.MirrorCS", {"start": v(-8, -50) * mm, "end": v(-3, -50) * mm});
            skLineSegment(sketch, "E332.MirrorCS", {"start": v(26, -55) * mm, "end": v(21, -55) * mm});
            skLineSegment(sketch, "E333.MirrorCS", {"start": v(26, -40.6) * mm, "end": v(26, -45.6) * mm});
            skLineSegment(sketch, "E334.MirrorCS", {"start": v(17, -21.8) * mm, "end": v(17, -26.8) * mm});
            skLineSegment(sketch, "E335.MirrorCS", {"start": v(30, -12.4) * mm, "end": v(30, -17.4) * mm});
            skLineSegment(sketch, "E336.MirrorCS", {"start": v(21, -31.2) * mm, "end": v(21, -36.2) * mm, "construction": true});
            skLineSegment(sketch, "E337.MirrorCS", {"start": v(-35, -55) * mm, "end": v(-30, -55) * mm});
            skLineSegment(sketch, "E338.MirrorCS", {"start": v(-30, -3) * mm, "end": v(-30, -8) * mm});
            skLineSegment(sketch, "E339.MirrorCS", {"start": v(-35, -40.6) * mm, "end": v(-35, -45.6) * mm});
            skLineSegment(sketch, "E340.MirrorCS", {"start": v(-35, -21.8) * mm, "end": v(-35, -26.8) * mm});
            skPoint(sketch, "E341.MirrorP", {"position": v(14.5, -24.3) * mm});
            skLineSegment(sketch, "E342.MirrorCS", {"start": v(30, -3) * mm, "end": v(30, -8) * mm});
            skLineSegment(sketch, "E343.MirrorCS", {"start": v(-26, -50) * mm, "end": v(-26, -55) * mm});
            skLineSegment(sketch, "E344.MirrorCS", {"start": v(-26, -8) * mm, "end": v(-21, -8) * mm});
            skPoint(sketch, "E345.MirrorP", {"position": v(23.5, -24.3) * mm});
            skPoint(sketch, "E346.MirrorP", {"position": v(-32.5, -5.5) * mm});
            skPoint(sketch, "E347.MirrorP", {"position": v(-32.5, -14.9) * mm});
            skLineSegment(sketch, "E348.MirrorCS", {"start": v(-3, -31.2) * mm, "end": v(-3, -36.2) * mm});
            skLineSegment(sketch, "E349.MirrorCS", {"start": v(8, -8) * mm, "end": v(3, -8) * mm, "construction": true});
            skLineSegment(sketch, "E350.MirrorCS", {"start": v(-35, -40.6) * mm, "end": v(-30, -40.6) * mm});
            skLineSegment(sketch, "E351.MirrorCS", {"start": v(-35, -3) * mm, "end": v(-30, -3) * mm});
            skLineSegment(sketch, "E352.MirrorCS", {"start": v(-8, -12.4) * mm, "end": v(-3, -12.4) * mm});
            skLineSegment(sketch, "E353.MirrorCS", {"start": v(-35, -50) * mm, "end": v(-35, -55) * mm});
            skLineSegment(sketch, "E354.MirrorCS", {"start": v(21, -21.8) * mm, "end": v(21, -26.8) * mm});
            skLineSegment(sketch, "E355.MirrorCS", {"start": v(3, -12.4) * mm, "end": v(3, -17.4) * mm});
            skLineSegment(sketch, "E356.MirrorCS", {"start": v(17, -3) * mm, "end": v(17, -8) * mm});
            skLineSegment(sketch, "E357.MirrorCS", {"start": v(-17, -12.4) * mm, "end": v(-17, -17.4) * mm});
            skLineSegment(sketch, "E358.MirrorCS", {"start": v(21, -50) * mm, "end": v(21, -55) * mm});
            skPoint(sketch, "E359.MirrorP", {"position": v(-14.5, -43.1) * mm});
            skPoint(sketch, "E360.MirrorP", {"position": v(-5.5, -33.7) * mm});
            skLineSegment(sketch, "E361.MirrorCS", {"start": v(30, -50) * mm, "end": v(21, -50) * mm, "construction": true});
            skLineSegment(sketch, "E362.MirrorCS", {"start": v(-30, -12.4) * mm, "end": v(-21, -12.4) * mm, "construction": true});
            skLineSegment(sketch, "E363.MirrorCS", {"start": v(-26, -21.8) * mm, "end": v(-26, -26.8) * mm});
            skPoint(sketch, "E364.MirrorP", {"position": v(32.5, -52.5) * mm});
            skLineSegment(sketch, "E365.MirrorCS", {"start": v(35, -36.2) * mm, "end": v(30, -36.2) * mm});
            skLineSegment(sketch, "E366.MirrorCS", {"start": v(-35, -3) * mm, "end": v(-35, -8) * mm});
            skLineSegment(sketch, "E367.MirrorCS", {"start": v(-30, -31.2) * mm, "end": v(-30, -36.2) * mm});
            skLineSegment(sketch, "E368.MirrorCS", {"start": v(-30, -40.6) * mm, "end": v(-30, -45.6) * mm});
            skLineSegment(sketch, "E369.MirrorCS", {"start": v(-26, -55) * mm, "end": v(-21, -55) * mm});
            skLineSegment(sketch, "E370.MirrorCS", {"start": v(-8, -36.2) * mm, "end": v(-3, -36.2) * mm});
            skLineSegment(sketch, "E371.MirrorCS", {"start": v(-8, -31.2) * mm, "end": v(-3, -31.2) * mm});
            skPoint(sketch, "E372.MirrorP", {"position": v(32.5, -24.3) * mm});
            skLineSegment(sketch, "E373.MirrorCS", {"start": v(-35, -21.8) * mm, "end": v(-30, -21.8) * mm});
            skLineSegment(sketch, "E374.MirrorCS", {"start": v(-26, -40.6) * mm, "end": v(-26, -45.6) * mm});
            skLineSegment(sketch, "E375.MirrorCS", {"start": v(-8, -8) * mm, "end": v(-3, -8) * mm, "construction": true});
            skLineSegment(sketch, "E376.MirrorCS", {"start": v(17, -45.6) * mm, "end": v(12, -45.6) * mm});
            skPoint(sketch, "E377.MirrorP", {"position": v(23.5, -43.1) * mm});
            skLineSegment(sketch, "E378.MirrorCS", {"start": v(26, -50) * mm, "end": v(26, -55) * mm});
            skLineSegment(sketch, "E379.MirrorCS", {"start": v(-12, -21.8) * mm, "end": v(-12, -26.8) * mm});
            skLineSegment(sketch, "E380.MirrorCS", {"start": v(-17, -31.2) * mm, "end": v(-17, -36.2) * mm});
            skLineSegment(sketch, "E381.MirrorCS", {"start": v(21, -12.4) * mm, "end": v(21, -17.4) * mm});
            skLineSegment(sketch, "E382.MirrorCS", {"start": v(17, -50) * mm, "end": v(17, -55) * mm});
            skLineSegment(sketch, "E383.MirrorCS", {"start": v(26, -45.6) * mm, "end": v(21, -45.6) * mm});
            skPoint(sketch, "E384.MirrorP", {"position": v(5.5, -43.1) * mm});
            skLineSegment(sketch, "E385.MirrorCS", {"start": v(8, -31.2) * mm, "end": v(8, -36.2) * mm});
            skLineSegment(sketch, "E386.MirrorCS", {"start": v(12, -21.8) * mm, "end": v(12, -26.8) * mm});
            skLineSegment(sketch, "E387.MirrorCS", {"start": v(-12, -40.6) * mm, "end": v(-12, -45.6) * mm});
            skLineSegment(sketch, "E388.MirrorCS", {"start": v(35, -26.8) * mm, "end": v(30, -26.8) * mm});
            skLineSegment(sketch, "E389.MirrorCS", {"start": v(-3, -21.8) * mm, "end": v(-3, -26.8) * mm});
            skLineSegment(sketch, "E390.MirrorCS", {"start": v(-17, -40.6) * mm, "end": v(-12, -40.6) * mm});
            skLineSegment(sketch, "E391.MirrorCS", {"start": v(-35, -26.8) * mm, "end": v(-30, -26.8) * mm});
            skLineSegment(sketch, "E392.MirrorCS", {"start": v(-35, -50) * mm, "end": v(-30, -50) * mm});
            skLineSegment(sketch, "E393.MirrorCS", {"start": v(21, -3) * mm, "end": v(21, -8) * mm});
            skLineSegment(sketch, "E394.MirrorCS", {"start": v(12, -31.2) * mm, "end": v(12, -36.2) * mm});
            skLineSegment(sketch, "E395.MirrorCS", {"start": v(-8, -55) * mm, "end": v(-3, -55) * mm});
            skLineSegment(sketch, "E396.MirrorCS", {"start": v(-17, -21.8) * mm, "end": v(-17, -26.8) * mm});
            skPoint(sketch, "E397.MirrorP", {"position": v(5.5, -14.9) * mm});
            skPoint(sketch, "E398.MirrorP", {"position": v(5.5, -5.5) * mm});
            skLineSegment(sketch, "E399.MirrorCS", {"start": v(-3, -12.4) * mm, "end": v(-3, -17.4) * mm});
            skPoint(sketch, "E400.MirrorP", {"position": v(-32.5, -24.3) * mm});
            skLineSegment(sketch, "E401.MirrorCS", {"start": v(35, -3) * mm, "end": v(35, -8) * mm});
            skLineSegment(sketch, "E402.MirrorCS", {"start": v(35, -40.6) * mm, "end": v(35, -45.6) * mm});
            skLineSegment(sketch, "E403.MirrorCS", {"start": v(-35, -12.4) * mm, "end": v(-30, -12.4) * mm});
            skLineSegment(sketch, "E404.MirrorCS", {"start": v(35, -31.2) * mm, "end": v(35, -36.2) * mm});
            skLineSegment(sketch, "E405.MirrorCS", {"start": v(-26, -45.6) * mm, "end": v(-21, -45.6) * mm});
            skPoint(sketch, "E406.MirrorP", {"position": v(14.5, -52.5) * mm});
            skPoint(sketch, "E407.MirrorP", {"position": v(23.5, -52.5) * mm});
            skLineSegment(sketch, "E408.MirrorCS", {"start": v(3, -3) * mm, "end": v(3, -8) * mm, "construction": true});
            skLineSegment(sketch, "E409.MirrorCS", {"start": v(-17, -3) * mm, "end": v(-17, -8) * mm});
            skLineSegment(sketch, "E410.MirrorCS", {"start": v(35, -12.4) * mm, "end": v(35, -17.4) * mm});
            skLineSegment(sketch, "E411.MirrorCS", {"start": v(12, -12.4) * mm, "end": v(12, -17.4) * mm});
            skLineSegment(sketch, "E412.MirrorCS", {"start": v(-17, -50) * mm, "end": v(-12, -50) * mm});
            skPoint(sketch, "E413.MirrorP", {"position": v(14.5, -14.9) * mm});
            skLineSegment(sketch, "E414.MirrorCS", {"start": v(35, -8) * mm, "end": v(30, -8) * mm});
            skLineSegment(sketch, "E415.MirrorCS", {"start": v(-8, -45.6) * mm, "end": v(-3, -45.6) * mm});
            skPoint(sketch, "E416.MirrorP", {"position": v(-14.5, -24.3) * mm});
            skLineSegment(sketch, "E417.MirrorCS", {"start": v(12, -40.6) * mm, "end": v(12, -45.6) * mm});
            skLineSegment(sketch, "E418.MirrorCS", {"start": v(-30, -12.4) * mm, "end": v(-30, -17.4) * mm});
            skLineSegment(sketch, "E419.MirrorCS", {"start": v(-26, -3) * mm, "end": v(-26, -8) * mm});
            skLineSegment(sketch, "E420.MirrorCS", {"start": v(-35, -8) * mm, "end": v(-30, -8) * mm});
            skSolve(sketch);
        }
        {
            var Q0;
            Q0=qSketchRegion(id+"F0",true);
            extrude(context, id + "F1", {"entities" : qUnion([Q0]), "depth" : 3 * mm, "offsetDistance" : 25 * mm});
        }
        {
            var Q0;
            Q0=qCreatedBy(makeId("Top.planeOp"),FACE);
            var sketch = newSketch(context, id + "F2", { "sketchPlane" : qUnion([Q0])});
            skLineSegment(sketch, "E421.rect.bottom", {"start": v(28, -57.05) * mm, "end": v(28, 27.95) * mm});
            skLineSegment(sketch, "E421.rect.top", {"start": v(-28, -57.05) * mm, "end": v(-28, 27.95) * mm});
            skLineSegment(sketch, "E421.rect.left", {"start": v(28, -57.05) * mm, "end": v(-28, -57.05) * mm});
            skLineSegment(sketch, "E421.rect.right", {"start": v(28, 27.95) * mm, "end": v(-28, 27.95) * mm});
            skPoint(sketch, "E421.rect.middle", {"position": v(0, -14.55) * mm});
            skLineSegment(sketch, "E422.rect.bottom", {"start": v(24.5, -33.55) * mm, "end": v(24.5, 24.45) * mm, "construction": true});
            skLineSegment(sketch, "E422.rect.top", {"start": v(-24.5, -33.55) * mm, "end": v(-24.5, 24.45) * mm, "construction": true});
            skLineSegment(sketch, "E422.rect.left", {"start": v(24.5, -33.55) * mm, "end": v(-24.5, -33.55) * mm, "construction": true});
            skLineSegment(sketch, "E422.rect.right", {"start": v(24.5, 24.45) * mm, "end": v(-24.5, 24.45) * mm, "construction": true});
            skPoint(sketch, "E422.rect.middle", {"position": v(0, -4.55) * mm});
            skCircle(sketch, "E423", {"center": v(-24.5, -33.55) * mm, "radius": 1.38 * mm});
            skCircle(sketch, "E424", {"center": v(-24.5, 24.45) * mm, "radius": 1.38 * mm});
            skCircle(sketch, "E425", {"center": v(24.5, 24.45) * mm, "radius": 1.38 * mm});
            skCircle(sketch, "E426", {"center": v(24.5, -33.55) * mm, "radius": 1.38 * mm});
            skSolve(sketch);
        }
        {
            var Q0;
            Q0=makeQuery(id+"F1.opExtrude","CAP_FACE",FACE,{"disambiguationData":[OSD([sQuery(id+"F0.wireOp",EDGE,"E2"),sQuery(id+"F0.wireOp",EDGE,"E3"),sQuery(id+"F0.wireOp",EDGE,"E4"),sQuery(id+"F0.wireOp",EDGE,"E5"),sQuery(id+"F0.wireOp",EDGE,"E6.MirrorCS"),sQuery(id+"F0.wireOp",EDGE,"E7.MirrorCS"),sQuery(id+"F0.wireOp",EDGE,"E8.MirrorCS"),sQuery(id+"F0.wireOp",EDGE,"E9.MirrorCS"),sQuery(id+"F0.wireOp",EDGE,"E10.MirrorCS"),sQuery(id+"F0.wireOp",EDGE,"E11"),sQuery(id+"F0.wireOp",EDGE,"E12"),sQuery(id+"F0.wireOp",EDGE,"E14.MirrorC"),sQuery(id+"F0.wireOp",EDGE,"E15.MirrorC"),sQuery(id+"F0.wireOp",EDGE,"E16"),sQuery(id+"F0.wireOp",EDGE,"E17"),sQuery(id+"F0.wireOp",EDGE,"E18.MirrorCS"),sQuery(id+"F0.wireOp",EDGE,"E19.MirrorCS"),sQuery(id+"F0.wireOp",EDGE,"E20.MirrorCS"),sQuery(id+"F0.wireOp",EDGE,"E21.MirrorCS"),sQuery(id+"F0.wireOp",EDGE,"E22.MirrorCS"),sQuery(id+"F0.wireOp",EDGE,"E23.MirrorCS"),sQuery(id+"F0.wireOp",EDGE,"E24.MirrorCS"),sQuery(id+"F0.wireOp",EDGE,"E25.MirrorCS"),sQuery(id+"F0.wireOp",EDGE,"E26.MirrorCS"),sQuery(id+"F0.wireOp",EDGE,"E27.MirrorCS"),sQuery(id+"F0.wireOp",EDGE,"E28.MirrorCS"),sQuery(id+"F0.wireOp",EDGE,"E29.MirrorCS"),sQuery(id+"F0.wireOp",EDGE,"E30.MirrorCS"),sQuery(id+"F0.wireOp",EDGE,"E31.MirrorC"),sQuery(id+"F0.wireOp",EDGE,"E32.MirrorC"),sQuery(id+"F0.wireOp",EDGE,"E33.MirrorC"),sQuery(id+"F0.wireOp",EDGE,"E34.MirrorC"),sQuery(id+"F0.wireOp",EDGE,"5c3mzxsr-oUSN-SXrm-x3ZU-d6UrBw8qLIhU.bottom"),sQuery(id+"F0.wireOp",EDGE,"5c3mzxsr-oUSN-SXrm-x3ZU-d6UrBw8qLIhU.top"),sQuery(id+"F0.wireOp",EDGE,"5c3mzxsr-oUSN-SXrm-x3ZU-d6UrBw8qLIhU.left"),sQuery(id+"F0.wireOp",EDGE,"5c3mzxsr-oUSN-SXrm-x3ZU-d6UrBw8qLIhU.right"),sQuery(id+"F0.wireOp",EDGE,"544fddae-270f-44da-af1d-2d8b63806ee7.1.0.0"),sQuery(id+"F0.wireOp",EDGE,"544fddae-270f-44da-af1d-2d8b63806ee7.1.0.1"),sQuery(id+"F0.wireOp",EDGE,"544fddae-270f-44da-af1d-2d8b63806ee7.1.0.2"),sQuery(id+"F0.wireOp",EDGE,"544fddae-270f-44da-af1d-2d8b63806ee7.1.0.3"),sQuery(id+"F0.wireOp",EDGE,"544fddae-270f-44da-af1d-2d8b63806ee7.2.0.0"),sQuery(id+"F0.wireOp",EDGE,"544fddae-270f-44da-af1d-2d8b63806ee7.2.0.1"),sQuery(id+"F0.wireOp",EDGE,"544fddae-270f-44da-af1d-2d8b63806ee7.2.0.2"),sQuery(id+"F0.wireOp",EDGE,"544fddae-270f-44da-af1d-2d8b63806ee7.2.0.3"),sQuery(id+"F0.wireOp",EDGE,"e76ad390-1c26-47f0-865e-979589794fca.0.3.0"),sQuery(id+"F0.wireOp",EDGE,"e76ad390-1c26-47f0-865e-979589794fca.3.3.0"),sQuery(id+"F0.wireOp",EDGE,"e76ad390-1c26-47f0-865e-979589794fca.6.3.0"),sQuery(id+"F0.wireOp",EDGE,"e76ad390-1c26-47f0-865e-979589794fca.9.3.0"),sQuery(id+"F0.wireOp",EDGE,"f5af7e2b-df8b-4b93-8138-36ea322a7ab3.1.0.0"),sQuery(id+"F0.wireOp",EDGE,"f5af7e2b-df8b-4b93-8138-36ea322a7ab3.1.0.1"),sQuery(id+"F0.wireOp",EDGE,"f5af7e2b-df8b-4b93-8138-36ea322a7ab3.1.0.2"),sQuery(id+"F0.wireOp",EDGE,"f5af7e2b-df8b-4b93-8138-36ea322a7ab3.1.0.3"),sQuery(id+"F0.wireOp",EDGE,"f5af7e2b-df8b-4b93-8138-36ea322a7ab3.1.0.4"),sQuery(id+"F0.wireOp",EDGE,"f5af7e2b-df8b-4b93-8138-36ea322a7ab3.1.0.5"),sQuery(id+"F0.wireOp",EDGE,"f5af7e2b-df8b-4b93-8138-36ea322a7ab3.1.0.6"),sQuery(id+"F0.wireOp",EDGE,"f5af7e2b-df8b-4b93-8138-36ea322a7ab3.1.0.7"),sQuery(id+"F0.wireOp",EDGE,"f5af7e2b-df8b-4b93-8138-36ea322a7ab3.1.0.8"),sQuery(id+"F0.wireOp",EDGE,"f5af7e2b-df8b-4b93-8138-36ea322a7ab3.1.0.9"),sQuery(id+"F0.wireOp",EDGE,"f5af7e2b-df8b-4b93-8138-36ea322a7ab3.1.0.10"),sQuery(id+"F0.wireOp",EDGE,"f5af7e2b-df8b-4b93-8138-36ea322a7ab3.1.0.11"),sQuery(id+"F0.wireOp",EDGE,"f5af7e2b-df8b-4b93-8138-36ea322a7ab3.1.0.12"),sQuery(id+"F0.wireOp",EDGE,"f5af7e2b-df8b-4b93-8138-36ea322a7ab3.1.0.13"),sQuery(id+"F0.wireOp",EDGE,"f5af7e2b-df8b-4b93-8138-36ea322a7ab3.1.0.14"),sQuery(id+"F0.wireOp",EDGE,"f5af7e2b-df8b-4b93-8138-36ea322a7ab3.1.0.15"),sQuery(id+"F0.wireOp",EDGE,"f5af7e2b-df8b-4b93-8138-36ea322a7ab3.2.0.0"),sQuery(id+"F0.wireOp",EDGE,"f5af7e2b-df8b-4b93-8138-36ea322a7ab3.2.0.1"),sQuery(id+"F0.wireOp",EDGE,"f5af7e2b-df8b-4b93-8138-36ea322a7ab3.2.0.2"),sQuery(id+"F0.wireOp",EDGE,"f5af7e2b-df8b-4b93-8138-36ea322a7ab3.2.0.3"),sQuery(id+"F0.wireOp",EDGE,"f5af7e2b-df8b-4b93-8138-36ea322a7ab3.2.0.4"),sQuery(id+"F0.wireOp",EDGE,"f5af7e2b-df8b-4b93-8138-36ea322a7ab3.2.0.5"),sQuery(id+"F0.wireOp",EDGE,"f5af7e2b-df8b-4b93-8138-36ea322a7ab3.2.0.6"),sQuery(id+"F0.wireOp",EDGE,"f5af7e2b-df8b-4b93-8138-36ea322a7ab3.2.0.7"),sQuery(id+"F0.wireOp",EDGE,"f5af7e2b-df8b-4b93-8138-36ea322a7ab3.2.0.8"),sQuery(id+"F0.wireOp",EDGE,"f5af7e2b-df8b-4b93-8138-36ea322a7ab3.2.0.9"),sQuery(id+"F0.wireOp",EDGE,"f5af7e2b-df8b-4b93-8138-36ea322a7ab3.2.0.10"),sQuery(id+"F0.wireOp",EDGE,"f5af7e2b-df8b-4b93-8138-36ea322a7ab3.2.0.11"),sQuery(id+"F0.wireOp",EDGE,"f5af7e2b-df8b-4b93-8138-36ea322a7ab3.2.0.12"),sQuery(id+"F0.wireOp",EDGE,"f5af7e2b-df8b-4b93-8138-36ea322a7ab3.2.0.13"),sQuery(id+"F0.wireOp",EDGE,"f5af7e2b-df8b-4b93-8138-36ea322a7ab3.2.0.14"),sQuery(id+"F0.wireOp",EDGE,"f5af7e2b-df8b-4b93-8138-36ea322a7ab3.2.0.15"),sQuery(id+"F0.wireOp",EDGE,"f5af7e2b-df8b-4b93-8138-36ea322a7ab3.3.0.0"),sQuery(id+"F0.wireOp",EDGE,"f5af7e2b-df8b-4b93-8138-36ea322a7ab3.3.0.1"),sQuery(id+"F0.wireOp",EDGE,"f5af7e2b-df8b-4b93-8138-36ea322a7ab3.3.0.2"),sQuery(id+"F0.wireOp",EDGE,"f5af7e2b-df8b-4b93-8138-36ea322a7ab3.3.0.3"),sQuery(id+"F0.wireOp",EDGE,"f5af7e2b-df8b-4b93-8138-36ea322a7ab3.3.0.5"),sQuery(id+"F0.wireOp",EDGE,"f5af7e2b-df8b-4b93-8138-36ea322a7ab3.3.0.6"),sQuery(id+"F0.wireOp",EDGE,"f5af7e2b-df8b-4b93-8138-36ea322a7ab3.3.0.7"),sQuery(id+"F0.wireOp",EDGE,"f5af7e2b-df8b-4b93-8138-36ea322a7ab3.3.0.8"),sQuery(id+"F0.wireOp",EDGE,"f5af7e2b-df8b-4b93-8138-36ea322a7ab3.3.0.10"),sQuery(id+"F0.wireOp",EDGE,"f5af7e2b-df8b-4b93-8138-36ea322a7ab3.3.0.11"),sQuery(id+"F0.wireOp",EDGE,"f5af7e2b-df8b-4b93-8138-36ea322a7ab3.3.0.13"),sQuery(id+"F0.wireOp",EDGE,"f5af7e2b-df8b-4b93-8138-36ea322a7ab3.3.0.14"),sQuery(id+"F0.wireOp",EDGE,"f5af7e2b-df8b-4b93-8138-36ea322a7ab3.4.0.0"),sQuery(id+"F0.wireOp",EDGE,"f5af7e2b-df8b-4b93-8138-36ea322a7ab3.4.0.1"),sQuery(id+"F0.wireOp",EDGE,"f5af7e2b-df8b-4b93-8138-36ea322a7ab3.4.0.2"),sQuery(id+"F0.wireOp",EDGE,"f5af7e2b-df8b-4b93-8138-36ea322a7ab3.4.0.3"),sQuery(id+"F0.wireOp",EDGE,"f5af7e2b-df8b-4b93-8138-36ea322a7ab3.4.0.4"),sQuery(id+"F0.wireOp",EDGE,"f5af7e2b-df8b-4b93-8138-36ea322a7ab3.4.0.5"),sQuery(id+"F0.wireOp",EDGE,"f5af7e2b-df8b-4b93-8138-36ea322a7ab3.4.0.6"),sQuery(id+"F0.wireOp",EDGE,"f5af7e2b-df8b-4b93-8138-36ea322a7ab3.4.0.7"),sQuery(id+"F0.wireOp",EDGE,"f5af7e2b-df8b-4b93-8138-36ea322a7ab3.4.0.8"),sQuery(id+"F0.wireOp",EDGE,"f5af7e2b-df8b-4b93-8138-36ea322a7ab3.4.0.9"),sQuery(id+"F0.wireOp",EDGE,"f5af7e2b-df8b-4b93-8138-36ea322a7ab3.4.0.10"),sQuery(id+"F0.wireOp",EDGE,"f5af7e2b-df8b-4b93-8138-36ea322a7ab3.4.0.11"),sQuery(id+"F0.wireOp",EDGE,"f5af7e2b-df8b-4b93-8138-36ea322a7ab3.4.0.12"),sQuery(id+"F0.wireOp",EDGE,"f5af7e2b-df8b-4b93-8138-36ea322a7ab3.4.0.13"),sQuery(id+"F0.wireOp",EDGE,"f5af7e2b-df8b-4b93-8138-36ea322a7ab3.4.0.14"),sQuery(id+"F0.wireOp",EDGE,"f5af7e2b-df8b-4b93-8138-36ea322a7ab3.4.0.15"),sQuery(id+"F0.wireOp",EDGE,"2337b784-ced5-4511-8511-f3861e9e9c320.MirrorCS"),sQuery(id+"F0.wireOp",EDGE,"2337b784-ced5-4511-8511-f3861e9e9c321.MirrorCS"),sQuery(id+"F0.wireOp",EDGE,"2337b784-ced5-4511-8511-f3861e9e9c322.MirrorCS"),sQuery(id+"F0.wireOp",EDGE,"2337b784-ced5-4511-8511-f3861e9e9c323.MirrorCS"),sQuery(id+"F0.wireOp",EDGE,"2337b784-ced5-4511-8511-f3861e9e9c324.MirrorCS"),sQuery(id+"F0.wireOp",EDGE,"2337b784-ced5-4511-8511-f3861e9e9c325.MirrorCS"),sQuery(id+"F0.wireOp",EDGE,"2337b784-ced5-4511-8511-f3861e9e9c326.MirrorCS"),sQuery(id+"F0.wireOp",EDGE,"2337b784-ced5-4511-8511-f3861e9e9c327.MirrorCS"),sQuery(id+"F0.wireOp",EDGE,"2337b784-ced5-4511-8511-f3861e9e9c328.MirrorCS"),sQuery(id+"F0.wireOp",EDGE,"2337b784-ced5-4511-8511-f3861e9e9c329.MirrorCS"),sQuery(id+"F0.wireOp",EDGE,"2337b784-ced5-4511-8511-f3861e9e9c3210.MirrorCS"),sQuery(id+"F0.wireOp",EDGE,"2337b784-ced5-4511-8511-f3861e9e9c3211.MirrorCS"),sQuery(id+"F0.wireOp",EDGE,"2337b784-ced5-4511-8511-f3861e9e9c3212.MirrorCS"),sQuery(id+"F0.wireOp",EDGE,"2337b784-ced5-4511-8511-f3861e9e9c3214.MirrorCS"),sQuery(id+"F0.wireOp",EDGE,"2337b784-ced5-4511-8511-f3861e9e9c3215.MirrorCS"),sQuery(id+"F0.wireOp",EDGE,"2337b784-ced5-4511-8511-f3861e9e9c3216.MirrorCS"),sQuery(id+"F0.wireOp",EDGE,"2337b784-ced5-4511-8511-f3861e9e9c3217.MirrorCS"),sQuery(id+"F0.wireOp",EDGE,"2337b784-ced5-4511-8511-f3861e9e9c3218.MirrorCS"),sQuery(id+"F0.wireOp",EDGE,"2337b784-ced5-4511-8511-f3861e9e9c3219.MirrorCS"),sQuery(id+"F0.wireOp",EDGE,"2337b784-ced5-4511-8511-f3861e9e9c3220.MirrorCS"),sQuery(id+"F0.wireOp",EDGE,"2337b784-ced5-4511-8511-f3861e9e9c3221.MirrorCS"),sQuery(id+"F0.wireOp",EDGE,"2337b784-ced5-4511-8511-f3861e9e9c3222.MirrorCS"),sQuery(id+"F0.wireOp",EDGE,"2337b784-ced5-4511-8511-f3861e9e9c3223.MirrorCS"),sQuery(id+"F0.wireOp",EDGE,"2337b784-ced5-4511-8511-f3861e9e9c3224.MirrorCS"),sQuery(id+"F0.wireOp",EDGE,"2337b784-ced5-4511-8511-f3861e9e9c3225.MirrorCS"),sQuery(id+"F0.wireOp",EDGE,"2337b784-ced5-4511-8511-f3861e9e9c3229.MirrorCS"),sQuery(id+"F0.wireOp",EDGE,"2337b784-ced5-4511-8511-f3861e9e9c3230.MirrorCS"),sQuery(id+"F0.wireOp",EDGE,"2337b784-ced5-4511-8511-f3861e9e9c3231.MirrorCS"),sQuery(id+"F0.wireOp",EDGE,"2337b784-ced5-4511-8511-f3861e9e9c3232.MirrorCS"),sQuery(id+"F0.wireOp",EDGE,"2337b784-ced5-4511-8511-f3861e9e9c3233.MirrorCS"),sQuery(id+"F0.wireOp",EDGE,"2337b784-ced5-4511-8511-f3861e9e9c3234.MirrorCS"),sQuery(id+"F0.wireOp",EDGE,"2337b784-ced5-4511-8511-f3861e9e9c3235.MirrorCS"),sQuery(id+"F0.wireOp",EDGE,"2337b784-ced5-4511-8511-f3861e9e9c3236.MirrorCS"),sQuery(id+"F0.wireOp",EDGE,"2337b784-ced5-4511-8511-f3861e9e9c3237.MirrorCS"),sQuery(id+"F0.wireOp",EDGE,"2337b784-ced5-4511-8511-f3861e9e9c3238.MirrorCS"),sQuery(id+"F0.wireOp",EDGE,"2337b784-ced5-4511-8511-f3861e9e9c3239.MirrorCS"),sQuery(id+"F0.wireOp",EDGE,"2337b784-ced5-4511-8511-f3861e9e9c3240.MirrorCS"),sQuery(id+"F0.wireOp",EDGE,"2337b784-ced5-4511-8511-f3861e9e9c3241.MirrorCS"),sQuery(id+"F0.wireOp",EDGE,"2337b784-ced5-4511-8511-f3861e9e9c3242.MirrorCS"),sQuery(id+"F0.wireOp",EDGE,"2337b784-ced5-4511-8511-f3861e9e9c3243.MirrorCS"),sQuery(id+"F0.wireOp",EDGE,"2337b784-ced5-4511-8511-f3861e9e9c3244.MirrorCS"),sQuery(id+"F0.wireOp",EDGE,"2337b784-ced5-4511-8511-f3861e9e9c3245.MirrorCS"),sQuery(id+"F0.wireOp",EDGE,"2337b784-ced5-4511-8511-f3861e9e9c3246.MirrorCS"),sQuery(id+"F0.wireOp",EDGE,"2337b784-ced5-4511-8511-f3861e9e9c3247.MirrorCS"),sQuery(id+"F0.wireOp",EDGE,"2337b784-ced5-4511-8511-f3861e9e9c3248.MirrorCS"),sQuery(id+"F0.wireOp",EDGE,"2337b784-ced5-4511-8511-f3861e9e9c3249.MirrorCS"),sQuery(id+"F0.wireOp",EDGE,"2337b784-ced5-4511-8511-f3861e9e9c3250.MirrorCS"),sQuery(id+"F0.wireOp",EDGE,"2337b784-ced5-4511-8511-f3861e9e9c3251.MirrorCS"),sQuery(id+"F0.wireOp",EDGE,"2337b784-ced5-4511-8511-f3861e9e9c3252.MirrorCS"),sQuery(id+"F0.wireOp",EDGE,"2337b784-ced5-4511-8511-f3861e9e9c3253.MirrorCS"),sQuery(id+"F0.wireOp",EDGE,"2337b784-ced5-4511-8511-f3861e9e9c3254.MirrorCS"),sQuery(id+"F0.wireOp",EDGE,"2337b784-ced5-4511-8511-f3861e9e9c3255.MirrorCS"),sQuery(id+"F0.wireOp",EDGE,"2337b784-ced5-4511-8511-f3861e9e9c3256.MirrorCS"),sQuery(id+"F0.wireOp",EDGE,"2337b784-ced5-4511-8511-f3861e9e9c3257.MirrorCS"),sQuery(id+"F0.wireOp",EDGE,"2337b784-ced5-4511-8511-f3861e9e9c3258.MirrorCS"),sQuery(id+"F0.wireOp",EDGE,"2337b784-ced5-4511-8511-f3861e9e9c3259.MirrorCS"),sQuery(id+"F0.wireOp",EDGE,"2337b784-ced5-4511-8511-f3861e9e9c3260.MirrorCS"),sQuery(id+"F0.wireOp",EDGE,"2337b784-ced5-4511-8511-f3861e9e9c3261.MirrorCS"),sQuery(id+"F0.wireOp",EDGE,"2337b784-ced5-4511-8511-f3861e9e9c3262.MirrorCS"),sQuery(id+"F0.wireOp",EDGE,"2337b784-ced5-4511-8511-f3861e9e9c3263.MirrorCS"),sQuery(id+"F0.wireOp",EDGE,"2337b784-ced5-4511-8511-f3861e9e9c3264.MirrorCS"),sQuery(id+"F0.wireOp",EDGE,"2337b784-ced5-4511-8511-f3861e9e9c3265.MirrorCS"),sQuery(id+"F0.wireOp",EDGE,"2337b784-ced5-4511-8511-f3861e9e9c3267.MirrorCS"),sQuery(id+"F0.wireOp",EDGE,"2337b784-ced5-4511-8511-f3861e9e9c3268.MirrorCS"),sQuery(id+"F0.wireOp",EDGE,"2337b784-ced5-4511-8511-f3861e9e9c3269.MirrorCS"),sQuery(id+"F0.wireOp",EDGE,"2337b784-ced5-4511-8511-f3861e9e9c3270.MirrorCS"),sQuery(id+"F0.wireOp",EDGE,"2337b784-ced5-4511-8511-f3861e9e9c3271.MirrorCS"),sQuery(id+"F0.wireOp",EDGE,"2337b784-ced5-4511-8511-f3861e9e9c3273.MirrorCS"),sQuery(id+"F0.wireOp",EDGE,"2337b784-ced5-4511-8511-f3861e9e9c3274.MirrorCS"),sQuery(id+"F0.wireOp",EDGE,"2337b784-ced5-4511-8511-f3861e9e9c3275.MirrorCS"),sQuery(id+"F0.wireOp",EDGE,"2337b784-ced5-4511-8511-f3861e9e9c3276.MirrorCS"),sQuery(id+"F0.wireOp",EDGE,"2337b784-ced5-4511-8511-f3861e9e9c3277.MirrorCS"),sQuery(id+"F0.wireOp",EDGE,"2337b784-ced5-4511-8511-f3861e9e9c3278.MirrorCS"),sQuery(id+"F0.wireOp",EDGE,"2337b784-ced5-4511-8511-f3861e9e9c3279.MirrorCS"),sQuery(id+"F0.wireOp",EDGE,"2337b784-ced5-4511-8511-f3861e9e9c3280.MirrorCS"),sQuery(id+"F0.wireOp",EDGE,"2337b784-ced5-4511-8511-f3861e9e9c3281.MirrorCS"),sQuery(id+"F0.wireOp",EDGE,"fa991f73-764b-433c-8341-ae9763ec17560.MirrorCS"),sQuery(id+"F0.wireOp",EDGE,"fa991f73-764b-433c-8341-ae9763ec17563.MirrorCS"),sQuery(id+"F0.wireOp",EDGE,"fa991f73-764b-433c-8341-ae9763ec17564.MirrorCS"),sQuery(id+"F0.wireOp",EDGE,"fa991f73-764b-433c-8341-ae9763ec17565.MirrorCS"),sQuery(id+"F0.wireOp",EDGE,"fa991f73-764b-433c-8341-ae9763ec17566.MirrorCS"),sQuery(id+"F0.wireOp",EDGE,"fa991f73-764b-433c-8341-ae9763ec17567.MirrorCS"),sQuery(id+"F0.wireOp",EDGE,"fa991f73-764b-433c-8341-ae9763ec17568.MirrorCS"),sQuery(id+"F0.wireOp",EDGE,"fa991f73-764b-433c-8341-ae9763ec17569.MirrorCS"),sQuery(id+"F0.wireOp",EDGE,"fa991f73-764b-433c-8341-ae9763ec175610.MirrorCS"),sQuery(id+"F0.wireOp",EDGE,"fa991f73-764b-433c-8341-ae9763ec175611.MirrorCS"),sQuery(id+"F0.wireOp",EDGE,"fa991f73-764b-433c-8341-ae9763ec175612.MirrorCS"),sQuery(id+"F0.wireOp",EDGE,"fa991f73-764b-433c-8341-ae9763ec175613.MirrorCS"),sQuery(id+"F0.wireOp",EDGE,"fa991f73-764b-433c-8341-ae9763ec175614.MirrorCS"),sQuery(id+"F0.wireOp",EDGE,"fa991f73-764b-433c-8341-ae9763ec175615.MirrorCS"),sQuery(id+"F0.wireOp",EDGE,"fa991f73-764b-433c-8341-ae9763ec175616.MirrorCS"),sQuery(id+"F0.wireOp",EDGE,"fa991f73-764b-433c-8341-ae9763ec175617.MirrorCS"),sQuery(id+"F0.wireOp",EDGE,"fa991f73-764b-433c-8341-ae9763ec175618.MirrorCS"),sQuery(id+"F0.wireOp",EDGE,"fa991f73-764b-433c-8341-ae9763ec175619.MirrorCS"),sQuery(id+"F0.wireOp",EDGE,"fa991f73-764b-433c-8341-ae9763ec175620.MirrorCS"),sQuery(id+"F0.wireOp",EDGE,"fa991f73-764b-433c-8341-ae9763ec175621.MirrorCS"),sQuery(id+"F0.wireOp",EDGE,"fa991f73-764b-433c-8341-ae9763ec175622.MirrorCS"),sQuery(id+"F0.wireOp",EDGE,"fa991f73-764b-433c-8341-ae9763ec175623.MirrorCS"),sQuery(id+"F0.wireOp",EDGE,"fa991f73-764b-433c-8341-ae9763ec175624.MirrorCS"),sQuery(id+"F0.wireOp",EDGE,"fa991f73-764b-433c-8341-ae9763ec175625.MirrorCS"),sQuery(id+"F0.wireOp",EDGE,"fa991f73-764b-433c-8341-ae9763ec175626.MirrorCS"),sQuery(id+"F0.wireOp",EDGE,"fa991f73-764b-433c-8341-ae9763ec175627.MirrorCS"),sQuery(id+"F0.wireOp",EDGE,"fa991f73-764b-433c-8341-ae9763ec175628.MirrorCS"),sQuery(id+"F0.wireOp",EDGE,"fa991f73-764b-433c-8341-ae9763ec175630.MirrorCS"),sQuery(id+"F0.wireOp",EDGE,"fa991f73-764b-433c-8341-ae9763ec175631.MirrorCS"),sQuery(id+"F0.wireOp",EDGE,"fa991f73-764b-433c-8341-ae9763ec175632.MirrorCS"),sQuery(id+"F0.wireOp",EDGE,"fa991f73-764b-433c-8341-ae9763ec175634.MirrorCS"),sQuery(id+"F0.wireOp",EDGE,"fa991f73-764b-433c-8341-ae9763ec175635.MirrorCS"),sQuery(id+"F0.wireOp",EDGE,"fa991f73-764b-433c-8341-ae9763ec175636.MirrorCS"),sQuery(id+"F0.wireOp",EDGE,"fa991f73-764b-433c-8341-ae9763ec175637.MirrorCS"),sQuery(id+"F0.wireOp",EDGE,"fa991f73-764b-433c-8341-ae9763ec175638.MirrorCS"),sQuery(id+"F0.wireOp",EDGE,"fa991f73-764b-433c-8341-ae9763ec175639.MirrorCS"),sQuery(id+"F0.wireOp",EDGE,"fa991f73-764b-433c-8341-ae9763ec175643.MirrorCS"),sQuery(id+"F0.wireOp",EDGE,"fa991f73-764b-433c-8341-ae9763ec175644.MirrorCS"),sQuery(id+"F0.wireOp",EDGE,"fa991f73-764b-433c-8341-ae9763ec175645.MirrorCS"),sQuery(id+"F0.wireOp",EDGE,"fa991f73-764b-433c-8341-ae9763ec175646.MirrorCS"),sQuery(id+"F0.wireOp",EDGE,"fa991f73-764b-433c-8341-ae9763ec175647.MirrorCS"),sQuery(id+"F0.wireOp",EDGE,"fa991f73-764b-433c-8341-ae9763ec175648.MirrorCS"),sQuery(id+"F0.wireOp",EDGE,"fa991f73-764b-433c-8341-ae9763ec175649.MirrorCS"),sQuery(id+"F0.wireOp",EDGE,"fa991f73-764b-433c-8341-ae9763ec175650.MirrorCS"),sQuery(id+"F0.wireOp",EDGE,"fa991f73-764b-433c-8341-ae9763ec175651.MirrorCS"),sQuery(id+"F0.wireOp",EDGE,"fa991f73-764b-433c-8341-ae9763ec175652.MirrorCS"),sQuery(id+"F0.wireOp",EDGE,"fa991f73-764b-433c-8341-ae9763ec175653.MirrorCS"),sQuery(id+"F0.wireOp",EDGE,"fa991f73-764b-433c-8341-ae9763ec175654.MirrorCS"),sQuery(id+"F0.wireOp",EDGE,"fa991f73-764b-433c-8341-ae9763ec175655.MirrorCS"),sQuery(id+"F0.wireOp",EDGE,"fa991f73-764b-433c-8341-ae9763ec175656.MirrorCS"),sQuery(id+"F0.wireOp",EDGE,"fa991f73-764b-433c-8341-ae9763ec175657.MirrorCS"),sQuery(id+"F0.wireOp",EDGE,"fa991f73-764b-433c-8341-ae9763ec175658.MirrorCS"),sQuery(id+"F0.wireOp",EDGE,"fa991f73-764b-433c-8341-ae9763ec175659.MirrorCS"),sQuery(id+"F0.wireOp",EDGE,"fa991f73-764b-433c-8341-ae9763ec175660.MirrorCS"),sQuery(id+"F0.wireOp",EDGE,"fa991f73-764b-433c-8341-ae9763ec175661.MirrorCS"),sQuery(id+"F0.wireOp",EDGE,"fa991f73-764b-433c-8341-ae9763ec175662.MirrorCS"),sQuery(id+"F0.wireOp",EDGE,"fa991f73-764b-433c-8341-ae9763ec175663.MirrorCS"),sQuery(id+"F0.wireOp",EDGE,"fa991f73-764b-433c-8341-ae9763ec175664.MirrorCS"),sQuery(id+"F0.wireOp",EDGE,"fa991f73-764b-433c-8341-ae9763ec175665.MirrorCS"),sQuery(id+"F0.wireOp",EDGE,"fa991f73-764b-433c-8341-ae9763ec175666.MirrorCS"),sQuery(id+"F0.wireOp",EDGE,"fa991f73-764b-433c-8341-ae9763ec175667.MirrorCS"),sQuery(id+"F0.wireOp",EDGE,"fa991f73-764b-433c-8341-ae9763ec175668.MirrorCS"),sQuery(id+"F0.wireOp",EDGE,"fa991f73-764b-433c-8341-ae9763ec175669.MirrorCS"),sQuery(id+"F0.wireOp",EDGE,"fa991f73-764b-433c-8341-ae9763ec175670.MirrorCS"),sQuery(id+"F0.wireOp",EDGE,"fa991f73-764b-433c-8341-ae9763ec175671.MirrorCS"),sQuery(id+"F0.wireOp",EDGE,"fa991f73-764b-433c-8341-ae9763ec175672.MirrorCS"),sQuery(id+"F0.wireOp",EDGE,"fa991f73-764b-433c-8341-ae9763ec175673.MirrorCS"),sQuery(id+"F0.wireOp",EDGE,"fa991f73-764b-433c-8341-ae9763ec175674.MirrorCS"),sQuery(id+"F0.wireOp",EDGE,"fa991f73-764b-433c-8341-ae9763ec175675.MirrorCS"),sQuery(id+"F0.wireOp",EDGE,"fa991f73-764b-433c-8341-ae9763ec175676.MirrorCS"),sQuery(id+"F0.wireOp",EDGE,"fa991f73-764b-433c-8341-ae9763ec175677.MirrorCS"),sQuery(id+"F0.wireOp",EDGE,"fa991f73-764b-433c-8341-ae9763ec175679.MirrorCS"),sQuery(id+"F0.wireOp",EDGE,"fa991f73-764b-433c-8341-ae9763ec175680.MirrorCS"),sQuery(id+"F0.wireOp",EDGE,"fa991f73-764b-433c-8341-ae9763ec175681.MirrorCS"),sQuery(id+"F0.wireOp",EDGE,"fa991f73-764b-433c-8341-ae9763ec175682.MirrorCS"),sQuery(id+"F0.wireOp",EDGE,"fa991f73-764b-433c-8341-ae9763ec175683.MirrorCS"),sQuery(id+"F0.wireOp",EDGE,"fa991f73-764b-433c-8341-ae9763ec175684.MirrorCS"),sQuery(id+"F0.wireOp",EDGE,"fa991f73-764b-433c-8341-ae9763ec175685.MirrorCS"),sQuery(id+"F0.wireOp",EDGE,"fa991f73-764b-433c-8341-ae9763ec175686.MirrorCS"),sQuery(id+"F0.wireOp",EDGE,"fa991f73-764b-433c-8341-ae9763ec175687.MirrorCS"),sQuery(id+"F0.wireOp",EDGE,"fa991f73-764b-433c-8341-ae9763ec175688.MirrorCS"),sQuery(id+"F0.wireOp",EDGE,"fa991f73-764b-433c-8341-ae9763ec175689.MirrorCS"),sQuery(id+"F0.wireOp",EDGE,"fa991f73-764b-433c-8341-ae9763ec175690.MirrorCS"),sQuery(id+"F0.wireOp",EDGE,"fa991f73-764b-433c-8341-ae9763ec175691.MirrorCS"),sQuery(id+"F0.wireOp",EDGE,"fa991f73-764b-433c-8341-ae9763ec175692.MirrorCS"),sQuery(id+"F0.wireOp",EDGE,"fa991f73-764b-433c-8341-ae9763ec175693.MirrorCS"),sQuery(id+"F0.wireOp",EDGE,"fa991f73-764b-433c-8341-ae9763ec175694.MirrorCS"),sQuery(id+"F0.wireOp",EDGE,"fa991f73-764b-433c-8341-ae9763ec175695.MirrorCS"),sQuery(id+"F0.wireOp",EDGE,"fa991f73-764b-433c-8341-ae9763ec175696.MirrorCS"),sQuery(id+"F0.wireOp",EDGE,"fa991f73-764b-433c-8341-ae9763ec175697.MirrorCS"),sQuery(id+"F0.wireOp",EDGE,"fa991f73-764b-433c-8341-ae9763ec175698.MirrorCS"),sQuery(id+"F0.wireOp",EDGE,"fa991f73-764b-433c-8341-ae9763ec175699.MirrorCS"),sQuery(id+"F0.wireOp",EDGE,"fa991f73-764b-433c-8341-ae9763ec1756100.MirrorCS"),sQuery(id+"F0.wireOp",EDGE,"fa991f73-764b-433c-8341-ae9763ec1756101.MirrorCS"),sQuery(id+"F0.wireOp",EDGE,"fa991f73-764b-433c-8341-ae9763ec1756102.MirrorCS"),sQuery(id+"F0.wireOp",EDGE,"fa991f73-764b-433c-8341-ae9763ec1756103.MirrorCS"),sQuery(id+"F0.wireOp",EDGE,"fa991f73-764b-433c-8341-ae9763ec1756104.MirrorCS"),sQuery(id+"F0.wireOp",EDGE,"fa991f73-764b-433c-8341-ae9763ec1756105.MirrorCS"),sQuery(id+"F0.wireOp",EDGE,"fa991f73-764b-433c-8341-ae9763ec1756106.MirrorCS"),sQuery(id+"F0.wireOp",EDGE,"fa991f73-764b-433c-8341-ae9763ec1756107.MirrorCS"),sQuery(id+"F0.wireOp",EDGE,"fa991f73-764b-433c-8341-ae9763ec1756108.MirrorCS"),sQuery(id+"F0.wireOp",EDGE,"fa991f73-764b-433c-8341-ae9763ec1756109.MirrorCS"),sQuery(id+"F0.wireOp",EDGE,"fa991f73-764b-433c-8341-ae9763ec1756110.MirrorCS"),sQuery(id+"F0.wireOp",EDGE,"fa991f73-764b-433c-8341-ae9763ec1756111.MirrorCS"),sQuery(id+"F0.wireOp",EDGE,"fa991f73-764b-433c-8341-ae9763ec1756112.MirrorCS"),sQuery(id+"F0.wireOp",EDGE,"fa991f73-764b-433c-8341-ae9763ec1756113.MirrorCS"),sQuery(id+"F0.wireOp",EDGE,"fa991f73-764b-433c-8341-ae9763ec1756114.MirrorCS"),sQuery(id+"F0.wireOp",EDGE,"fa991f73-764b-433c-8341-ae9763ec1756116.MirrorCS"),sQuery(id+"F0.wireOp",EDGE,"fa991f73-764b-433c-8341-ae9763ec1756117.MirrorCS"),sQuery(id+"F0.wireOp",EDGE,"fa991f73-764b-433c-8341-ae9763ec1756118.MirrorCS"),sQuery(id+"F0.wireOp",EDGE,"fa991f73-764b-433c-8341-ae9763ec1756119.MirrorCS"),sQuery(id+"F0.wireOp",EDGE,"fa991f73-764b-433c-8341-ae9763ec1756120.MirrorCS"),sQuery(id+"F0.wireOp",EDGE,"fa991f73-764b-433c-8341-ae9763ec1756121.MirrorCS"),sQuery(id+"F0.wireOp",EDGE,"fa991f73-764b-433c-8341-ae9763ec1756122.MirrorCS"),sQuery(id+"F0.wireOp",EDGE,"fa991f73-764b-433c-8341-ae9763ec1756123.MirrorCS"),sQuery(id+"F0.wireOp",EDGE,"fa991f73-764b-433c-8341-ae9763ec1756124.MirrorCS"),sQuery(id+"F0.wireOp",EDGE,"fa991f73-764b-433c-8341-ae9763ec1756125.MirrorCS"),sQuery(id+"F0.wireOp",EDGE,"fa991f73-764b-433c-8341-ae9763ec1756127.MirrorCS"),sQuery(id+"F0.wireOp",EDGE,"fa991f73-764b-433c-8341-ae9763ec1756128.MirrorCS"),sQuery(id+"F0.wireOp",EDGE,"fa991f73-764b-433c-8341-ae9763ec1756129.MirrorCS"),sQuery(id+"F0.wireOp",EDGE,"fa991f73-764b-433c-8341-ae9763ec1756130.MirrorCS"),sQuery(id+"F0.wireOp",EDGE,"fa991f73-764b-433c-8341-ae9763ec1756131.MirrorCS"),sQuery(id+"F0.wireOp",EDGE,"fa991f73-764b-433c-8341-ae9763ec1756132.MirrorCS"),sQuery(id+"F0.wireOp",EDGE,"fa991f73-764b-433c-8341-ae9763ec1756133.MirrorCS"),sQuery(id+"F0.wireOp",EDGE,"fa991f73-764b-433c-8341-ae9763ec1756134.MirrorCS"),sQuery(id+"F0.wireOp",EDGE,"fa991f73-764b-433c-8341-ae9763ec1756135.MirrorCS"),sQuery(id+"F0.wireOp",EDGE,"fa991f73-764b-433c-8341-ae9763ec1756137.MirrorCS"),sQuery(id+"F0.wireOp",EDGE,"fa991f73-764b-433c-8341-ae9763ec1756138.MirrorCS"),sQuery(id+"F0.wireOp",EDGE,"fa991f73-764b-433c-8341-ae9763ec1756139.MirrorCS"),sQuery(id+"F0.wireOp",EDGE,"fa991f73-764b-433c-8341-ae9763ec1756140.MirrorCS"),sQuery(id+"F0.wireOp",EDGE,"fa991f73-764b-433c-8341-ae9763ec1756141.MirrorCS"),sQuery(id+"F0.wireOp",EDGE,"fa991f73-764b-433c-8341-ae9763ec1756142.MirrorCS"),sQuery(id+"F0.wireOp",EDGE,"fa991f73-764b-433c-8341-ae9763ec1756143.MirrorCS"),sQuery(id+"F0.wireOp",EDGE,"fa991f73-764b-433c-8341-ae9763ec1756144.MirrorCS"),sQuery(id+"F0.wireOp",EDGE,"fa991f73-764b-433c-8341-ae9763ec1756145.MirrorCS"),sQuery(id+"F0.wireOp",EDGE,"fa991f73-764b-433c-8341-ae9763ec1756146.MirrorCS"),sQuery(id+"F0.wireOp",EDGE,"fa991f73-764b-433c-8341-ae9763ec1756147.MirrorCS"),sQuery(id+"F0.wireOp",EDGE,"fa991f73-764b-433c-8341-ae9763ec1756148.MirrorCS"),sQuery(id+"F0.wireOp",EDGE,"fa991f73-764b-433c-8341-ae9763ec1756149.MirrorCS"),sQuery(id+"F0.wireOp",EDGE,"fa991f73-764b-433c-8341-ae9763ec1756150.MirrorCS"),sQuery(id+"F0.wireOp",EDGE,"fa991f73-764b-433c-8341-ae9763ec1756151.MirrorCS"),sQuery(id+"F0.wireOp",EDGE,"fa991f73-764b-433c-8341-ae9763ec1756152.MirrorCS"),sQuery(id+"F0.wireOp",EDGE,"fa991f73-764b-433c-8341-ae9763ec1756153.MirrorCS"),sQuery(id+"F0.wireOp",EDGE,"fa991f73-764b-433c-8341-ae9763ec1756154.MirrorCS"),sQuery(id+"F0.wireOp",EDGE,"fa991f73-764b-433c-8341-ae9763ec1756155.MirrorCS"),sQuery(id+"F0.wireOp",EDGE,"fa991f73-764b-433c-8341-ae9763ec1756157.MirrorCS"),sQuery(id+"F0.wireOp",EDGE,"fa991f73-764b-433c-8341-ae9763ec1756158.MirrorCS"),sQuery(id+"F0.wireOp",EDGE,"fa991f73-764b-433c-8341-ae9763ec1756159.MirrorCS"),sQuery(id+"F0.wireOp",EDGE,"fa991f73-764b-433c-8341-ae9763ec1756160.MirrorCS"),sQuery(id+"F0.wireOp",EDGE,"fa991f73-764b-433c-8341-ae9763ec1756161.MirrorCS"),sQuery(id+"F0.wireOp",EDGE,"fa991f73-764b-433c-8341-ae9763ec1756162.MirrorCS"),sQuery(id+"F0.wireOp",EDGE,"fa991f73-764b-433c-8341-ae9763ec1756163.MirrorCS")])],"isStart":false});
            var sketch = newSketch(context, id + "F3", { "sketchPlane" : qUnion([Q0])});
            skCircle(sketch, "E427", {"center": v(24.5, 24.45) * mm, "radius": 1.25 * mm});
            skCircle(sketch, "E428", {"center": v(-24.5, 24.45) * mm, "radius": 1.25 * mm});
            skCircle(sketch, "E429", {"center": v(-24.5, -33.55) * mm, "radius": 1.25 * mm});
            skCircle(sketch, "E430", {"center": v(24.5, -33.55) * mm, "radius": 1.25 * mm});
            skSolve(sketch);
        }
        {
            var Q0;
            Q0=makeQuery(id+"F3.imprint","IMPRINT",FACE,{"disambiguationData":[TD([[makeQuery(id+"F3.imprint","IMPRINT",EDGE,{"derivedFrom":sQuery(id+"F3.wireOp",EDGE,"E427")}),-1.0]])]});
            var sketch = newSketch(context, id + "F4", { "sketchPlane" : qUnion([Q0])});
            skPoint(sketch, "E431", {"position": v(-20.32, 52.88) * mm});
            skPoint(sketch, "E432", {"position": v(-20.32, 68.12) * mm});
            skPoint(sketch, "E433", {"position": v(20.32, 52.88) * mm});
            skPoint(sketch, "E434", {"position": v(20.32, 68.12) * mm});
            skLineSegment(sketch, "E435", {"start": v(21.77, 51.61) * mm, "end": v(-21.41, 51.6) * mm});
            skLineSegment(sketch, "E436", {"start": v(-21.41, 51.6) * mm, "end": v(-21.41, 69.39) * mm});
            skLineSegment(sketch, "E437", {"start": v(-21.41, 69.39) * mm, "end": v(21.77, 69.4) * mm});
            skLineSegment(sketch, "E438", {"start": v(21.77, 69.4) * mm, "end": v(21.77, 51.61) * mm});
            skCircle(sketch, "E439", {"center": v(-20.32, 52.88) * mm, "radius": 0.6 * mm});
            skCircle(sketch, "E440", {"center": v(-20.32, 68.12) * mm, "radius": 0.6 * mm});
            skCircle(sketch, "E441", {"center": v(20.32, 68.12) * mm, "radius": 0.6 * mm});
            skCircle(sketch, "E442", {"center": v(20.32, 52.88) * mm, "radius": 0.6 * mm});
            skLineSegment(sketch, "E443", {"start": v(-20.32, 68.12) * mm, "end": v(20.32, 52.88) * mm, "construction": true});
            skLineSegment(sketch, "E444", {"start": v(20.32, 68.12) * mm, "end": v(-20.32, 52.88) * mm, "construction": true});
            skPoint(sketch, "E445", {"position": v(0, 60.5) * mm});
            skSolve(sketch);
        }
        {
            var Q0;
            Q0=qSketchRegion(id+"F3",true);
            extrude(context, id + "F5", {"entities" : qUnion([Q0]), "operationType" : NewBodyOperationType.REMOVE, "oppositeDirection" : true, "depth" : 5 * mm, "offsetDistance" : 25 * mm});
        }
        {
            var Q0;
            Q0=makeQuery(id+"F4.imprint","IMPRINT",FACE,{"disambiguationData":[TD([[makeQuery(id+"F4.imprint","IMPRINT",EDGE,{"derivedFrom":sQuery(id+"F4.wireOp",EDGE,"E439")}),1.0]])]});
            var Q1;
            Q1=makeQuery(id+"F4.imprint","IMPRINT",FACE,{"disambiguationData":[TD([[makeQuery(id+"F4.imprint","IMPRINT",EDGE,{"derivedFrom":sQuery(id+"F4.wireOp",EDGE,"E440")}),1.0]])]});
            var Q2;
            Q2=makeQuery(id+"F4.imprint","IMPRINT",FACE,{"disambiguationData":[TD([[makeQuery(id+"F4.imprint","IMPRINT",EDGE,{"derivedFrom":sQuery(id+"F4.wireOp",EDGE,"E441")}),1.0]])]});
            var Q3;
            Q3=makeQuery(id+"F4.imprint","IMPRINT",FACE,{"disambiguationData":[TD([[makeQuery(id+"F4.imprint","IMPRINT",EDGE,{"derivedFrom":sQuery(id+"F4.wireOp",EDGE,"E442")}),1.0]])]});
            var Q4;
            Q4=sQuery(id+"F4.wireOp",EDGE,"E439");
            extrude(context, id + "F6", {"entities" : qUnion([Q0, Q1, Q2, Q3]), "operationType" : NewBodyOperationType.REMOVE, "surfaceEntities" : qUnion([Q4]), "oppositeDirection" : true, "depth" : 5 * mm, "offsetDistance" : 25 * mm});
        }
        {
            var Q0;
            Q0=makeQuery(id+"F1.opExtrude","CAP_FACE",FACE,{"disambiguationData":[OSD([sQuery(id+"F0.wireOp",EDGE,"E2"),sQuery(id+"F0.wireOp",EDGE,"E3"),sQuery(id+"F0.wireOp",EDGE,"E4"),sQuery(id+"F0.wireOp",EDGE,"E5"),sQuery(id+"F0.wireOp",EDGE,"E6.MirrorCS"),sQuery(id+"F0.wireOp",EDGE,"E7.MirrorCS"),sQuery(id+"F0.wireOp",EDGE,"E8.MirrorCS"),sQuery(id+"F0.wireOp",EDGE,"E9.MirrorCS"),sQuery(id+"F0.wireOp",EDGE,"E10.MirrorCS"),sQuery(id+"F0.wireOp",EDGE,"E11"),sQuery(id+"F0.wireOp",EDGE,"E12"),sQuery(id+"F0.wireOp",EDGE,"E14.MirrorC"),sQuery(id+"F0.wireOp",EDGE,"E15.MirrorC"),sQuery(id+"F0.wireOp",EDGE,"E16"),sQuery(id+"F0.wireOp",EDGE,"E17"),sQuery(id+"F0.wireOp",EDGE,"E18.MirrorCS"),sQuery(id+"F0.wireOp",EDGE,"E19.MirrorCS"),sQuery(id+"F0.wireOp",EDGE,"E20.MirrorCS"),sQuery(id+"F0.wireOp",EDGE,"E21.MirrorCS"),sQuery(id+"F0.wireOp",EDGE,"E22.MirrorCS"),sQuery(id+"F0.wireOp",EDGE,"E23.MirrorCS"),sQuery(id+"F0.wireOp",EDGE,"E24.MirrorCS"),sQuery(id+"F0.wireOp",EDGE,"E25.MirrorCS"),sQuery(id+"F0.wireOp",EDGE,"E26.MirrorCS"),sQuery(id+"F0.wireOp",EDGE,"E27.MirrorCS"),sQuery(id+"F0.wireOp",EDGE,"E28.MirrorCS"),sQuery(id+"F0.wireOp",EDGE,"E29.MirrorCS"),sQuery(id+"F0.wireOp",EDGE,"E30.MirrorCS"),sQuery(id+"F0.wireOp",EDGE,"E31.MirrorC"),sQuery(id+"F0.wireOp",EDGE,"E32.MirrorC"),sQuery(id+"F0.wireOp",EDGE,"E33.MirrorC"),sQuery(id+"F0.wireOp",EDGE,"E34.MirrorC"),sQuery(id+"F0.wireOp",EDGE,"68b7a1c4-8bc2-4b87-af8e-2383ff06fe301.MirrorCS"),sQuery(id+"F0.wireOp",EDGE,"68b7a1c4-8bc2-4b87-af8e-2383ff06fe302.MirrorCS"),sQuery(id+"F0.wireOp",EDGE,"68b7a1c4-8bc2-4b87-af8e-2383ff06fe303.MirrorCS"),sQuery(id+"F0.wireOp",EDGE,"68b7a1c4-8bc2-4b87-af8e-2383ff06fe304.MirrorCS"),sQuery(id+"F0.wireOp",EDGE,"68b7a1c4-8bc2-4b87-af8e-2383ff06fe305.MirrorCS"),sQuery(id+"F0.wireOp",EDGE,"68b7a1c4-8bc2-4b87-af8e-2383ff06fe306.MirrorCS"),sQuery(id+"F0.wireOp",EDGE,"68b7a1c4-8bc2-4b87-af8e-2383ff06fe307.MirrorCS"),sQuery(id+"F0.wireOp",EDGE,"68b7a1c4-8bc2-4b87-af8e-2383ff06fe308.MirrorCS"),sQuery(id+"F0.wireOp",EDGE,"68b7a1c4-8bc2-4b87-af8e-2383ff06fe309.MirrorCS"),sQuery(id+"F0.wireOp",EDGE,"68b7a1c4-8bc2-4b87-af8e-2383ff06fe3010.MirrorCS"),sQuery(id+"F0.wireOp",EDGE,"68b7a1c4-8bc2-4b87-af8e-2383ff06fe3011.MirrorCS"),sQuery(id+"F0.wireOp",EDGE,"68b7a1c4-8bc2-4b87-af8e-2383ff06fe3012.MirrorCS"),sQuery(id+"F0.wireOp",EDGE,"68b7a1c4-8bc2-4b87-af8e-2383ff06fe3013.MirrorCS"),sQuery(id+"F0.wireOp",EDGE,"68b7a1c4-8bc2-4b87-af8e-2383ff06fe3014.MirrorCS"),sQuery(id+"F0.wireOp",EDGE,"68b7a1c4-8bc2-4b87-af8e-2383ff06fe3015.MirrorCS"),sQuery(id+"F0.wireOp",EDGE,"68b7a1c4-8bc2-4b87-af8e-2383ff06fe3016.MirrorCS"),sQuery(id+"F0.wireOp",EDGE,"68b7a1c4-8bc2-4b87-af8e-2383ff06fe3017.MirrorCS"),sQuery(id+"F0.wireOp",EDGE,"68b7a1c4-8bc2-4b87-af8e-2383ff06fe3018.MirrorCS"),sQuery(id+"F0.wireOp",EDGE,"68b7a1c4-8bc2-4b87-af8e-2383ff06fe3019.MirrorCS"),sQuery(id+"F0.wireOp",EDGE,"68b7a1c4-8bc2-4b87-af8e-2383ff06fe3020.MirrorCS"),sQuery(id+"F0.wireOp",EDGE,"68b7a1c4-8bc2-4b87-af8e-2383ff06fe3021.MirrorCS"),sQuery(id+"F0.wireOp",EDGE,"68b7a1c4-8bc2-4b87-af8e-2383ff06fe3022.MirrorCS"),sQuery(id+"F0.wireOp",EDGE,"68b7a1c4-8bc2-4b87-af8e-2383ff06fe3023.MirrorCS"),sQuery(id+"F0.wireOp",EDGE,"68b7a1c4-8bc2-4b87-af8e-2383ff06fe3024.MirrorCS"),sQuery(id+"F0.wireOp",EDGE,"68b7a1c4-8bc2-4b87-af8e-2383ff06fe3025.MirrorCS"),sQuery(id+"F0.wireOp",EDGE,"68b7a1c4-8bc2-4b87-af8e-2383ff06fe3026.MirrorCS"),sQuery(id+"F0.wireOp",EDGE,"68b7a1c4-8bc2-4b87-af8e-2383ff06fe3027.MirrorCS"),sQuery(id+"F0.wireOp",EDGE,"68b7a1c4-8bc2-4b87-af8e-2383ff06fe3028.MirrorCS"),sQuery(id+"F0.wireOp",EDGE,"68b7a1c4-8bc2-4b87-af8e-2383ff06fe3029.MirrorCS"),sQuery(id+"F0.wireOp",EDGE,"68b7a1c4-8bc2-4b87-af8e-2383ff06fe3030.MirrorCS"),sQuery(id+"F0.wireOp",EDGE,"68b7a1c4-8bc2-4b87-af8e-2383ff06fe3031.MirrorCS"),sQuery(id+"F0.wireOp",EDGE,"68b7a1c4-8bc2-4b87-af8e-2383ff06fe3032.MirrorCS"),sQuery(id+"F0.wireOp",EDGE,"68b7a1c4-8bc2-4b87-af8e-2383ff06fe3033.MirrorCS"),sQuery(id+"F0.wireOp",EDGE,"68b7a1c4-8bc2-4b87-af8e-2383ff06fe3034.MirrorCS"),sQuery(id+"F0.wireOp",EDGE,"68b7a1c4-8bc2-4b87-af8e-2383ff06fe3035.MirrorCS"),sQuery(id+"F0.wireOp",EDGE,"68b7a1c4-8bc2-4b87-af8e-2383ff06fe3036.MirrorCS"),sQuery(id+"F0.wireOp",EDGE,"68b7a1c4-8bc2-4b87-af8e-2383ff06fe3037.MirrorCS"),sQuery(id+"F0.wireOp",EDGE,"68b7a1c4-8bc2-4b87-af8e-2383ff06fe3038.MirrorCS"),sQuery(id+"F0.wireOp",EDGE,"68b7a1c4-8bc2-4b87-af8e-2383ff06fe3039.MirrorCS"),sQuery(id+"F0.wireOp",EDGE,"68b7a1c4-8bc2-4b87-af8e-2383ff06fe3040.MirrorCS"),sQuery(id+"F0.wireOp",EDGE,"68b7a1c4-8bc2-4b87-af8e-2383ff06fe3041.MirrorCS"),sQuery(id+"F0.wireOp",EDGE,"68b7a1c4-8bc2-4b87-af8e-2383ff06fe3042.MirrorCS"),sQuery(id+"F0.wireOp",EDGE,"68b7a1c4-8bc2-4b87-af8e-2383ff06fe3043.MirrorCS"),sQuery(id+"F0.wireOp",EDGE,"68b7a1c4-8bc2-4b87-af8e-2383ff06fe3044.MirrorCS"),sQuery(id+"F0.wireOp",EDGE,"68b7a1c4-8bc2-4b87-af8e-2383ff06fe3045.MirrorCS"),sQuery(id+"F0.wireOp",EDGE,"68b7a1c4-8bc2-4b87-af8e-2383ff06fe3046.MirrorCS"),sQuery(id+"F0.wireOp",EDGE,"68b7a1c4-8bc2-4b87-af8e-2383ff06fe3048.MirrorCS"),sQuery(id+"F0.wireOp",EDGE,"68b7a1c4-8bc2-4b87-af8e-2383ff06fe3049.MirrorCS"),sQuery(id+"F0.wireOp",EDGE,"68b7a1c4-8bc2-4b87-af8e-2383ff06fe3050.MirrorCS"),sQuery(id+"F0.wireOp",EDGE,"68b7a1c4-8bc2-4b87-af8e-2383ff06fe3051.MirrorCS"),sQuery(id+"F0.wireOp",EDGE,"68b7a1c4-8bc2-4b87-af8e-2383ff06fe3052.MirrorCS"),sQuery(id+"F0.wireOp",EDGE,"68b7a1c4-8bc2-4b87-af8e-2383ff06fe3053.MirrorCS"),sQuery(id+"F0.wireOp",EDGE,"68b7a1c4-8bc2-4b87-af8e-2383ff06fe3054.MirrorCS"),sQuery(id+"F0.wireOp",EDGE,"68b7a1c4-8bc2-4b87-af8e-2383ff06fe3055.MirrorCS"),sQuery(id+"F0.wireOp",EDGE,"68b7a1c4-8bc2-4b87-af8e-2383ff06fe3057.MirrorCS"),sQuery(id+"F0.wireOp",EDGE,"68b7a1c4-8bc2-4b87-af8e-2383ff06fe3058.MirrorCS"),sQuery(id+"F0.wireOp",EDGE,"68b7a1c4-8bc2-4b87-af8e-2383ff06fe3059.MirrorCS"),sQuery(id+"F0.wireOp",EDGE,"68b7a1c4-8bc2-4b87-af8e-2383ff06fe3061.MirrorCS"),sQuery(id+"F0.wireOp",EDGE,"68b7a1c4-8bc2-4b87-af8e-2383ff06fe3062.MirrorCS"),sQuery(id+"F0.wireOp",EDGE,"68b7a1c4-8bc2-4b87-af8e-2383ff06fe3063.MirrorCS"),sQuery(id+"F0.wireOp",EDGE,"68b7a1c4-8bc2-4b87-af8e-2383ff06fe3064.MirrorCS"),sQuery(id+"F0.wireOp",EDGE,"68b7a1c4-8bc2-4b87-af8e-2383ff06fe3065.MirrorCS"),sQuery(id+"F0.wireOp",EDGE,"68b7a1c4-8bc2-4b87-af8e-2383ff06fe3066.MirrorCS"),sQuery(id+"F0.wireOp",EDGE,"68b7a1c4-8bc2-4b87-af8e-2383ff06fe3067.MirrorCS"),sQuery(id+"F0.wireOp",EDGE,"68b7a1c4-8bc2-4b87-af8e-2383ff06fe3068.MirrorCS"),sQuery(id+"F0.wireOp",EDGE,"68b7a1c4-8bc2-4b87-af8e-2383ff06fe3069.MirrorCS"),sQuery(id+"F0.wireOp",EDGE,"68b7a1c4-8bc2-4b87-af8e-2383ff06fe3070.MirrorCS"),sQuery(id+"F0.wireOp",EDGE,"68b7a1c4-8bc2-4b87-af8e-2383ff06fe3071.MirrorCS"),sQuery(id+"F0.wireOp",EDGE,"68b7a1c4-8bc2-4b87-af8e-2383ff06fe3072.MirrorCS"),sQuery(id+"F0.wireOp",EDGE,"68b7a1c4-8bc2-4b87-af8e-2383ff06fe3073.MirrorCS"),sQuery(id+"F0.wireOp",EDGE,"68b7a1c4-8bc2-4b87-af8e-2383ff06fe3074.MirrorCS"),sQuery(id+"F0.wireOp",EDGE,"68b7a1c4-8bc2-4b87-af8e-2383ff06fe3075.MirrorCS"),sQuery(id+"F0.wireOp",EDGE,"68b7a1c4-8bc2-4b87-af8e-2383ff06fe3076.MirrorCS"),sQuery(id+"F0.wireOp",EDGE,"68b7a1c4-8bc2-4b87-af8e-2383ff06fe3078.MirrorCS"),sQuery(id+"F0.wireOp",EDGE,"68b7a1c4-8bc2-4b87-af8e-2383ff06fe3079.MirrorCS"),sQuery(id+"F0.wireOp",EDGE,"68b7a1c4-8bc2-4b87-af8e-2383ff06fe3080.MirrorCS"),sQuery(id+"F0.wireOp",EDGE,"68b7a1c4-8bc2-4b87-af8e-2383ff06fe3081.MirrorCS"),sQuery(id+"F0.wireOp",EDGE,"68b7a1c4-8bc2-4b87-af8e-2383ff06fe3082.MirrorCS"),sQuery(id+"F0.wireOp",EDGE,"68b7a1c4-8bc2-4b87-af8e-2383ff06fe3083.MirrorCS"),sQuery(id+"F0.wireOp",EDGE,"68b7a1c4-8bc2-4b87-af8e-2383ff06fe3085.MirrorCS"),sQuery(id+"F0.wireOp",EDGE,"68b7a1c4-8bc2-4b87-af8e-2383ff06fe3086.MirrorCS"),sQuery(id+"F0.wireOp",EDGE,"68b7a1c4-8bc2-4b87-af8e-2383ff06fe3087.MirrorCS"),sQuery(id+"F0.wireOp",EDGE,"68b7a1c4-8bc2-4b87-af8e-2383ff06fe3091.MirrorCS"),sQuery(id+"F0.wireOp",EDGE,"68b7a1c4-8bc2-4b87-af8e-2383ff06fe3092.MirrorCS"),sQuery(id+"F0.wireOp",EDGE,"68b7a1c4-8bc2-4b87-af8e-2383ff06fe3094.MirrorCS"),sQuery(id+"F0.wireOp",EDGE,"68b7a1c4-8bc2-4b87-af8e-2383ff06fe3095.MirrorCS"),sQuery(id+"F0.wireOp",EDGE,"68b7a1c4-8bc2-4b87-af8e-2383ff06fe3096.MirrorCS"),sQuery(id+"F0.wireOp",EDGE,"68b7a1c4-8bc2-4b87-af8e-2383ff06fe3097.MirrorCS"),sQuery(id+"F0.wireOp",EDGE,"68b7a1c4-8bc2-4b87-af8e-2383ff06fe3098.MirrorCS"),sQuery(id+"F0.wireOp",EDGE,"68b7a1c4-8bc2-4b87-af8e-2383ff06fe3099.MirrorCS"),sQuery(id+"F0.wireOp",EDGE,"68b7a1c4-8bc2-4b87-af8e-2383ff06fe30100.MirrorCS"),sQuery(id+"F0.wireOp",EDGE,"68b7a1c4-8bc2-4b87-af8e-2383ff06fe30101.MirrorCS"),sQuery(id+"F0.wireOp",EDGE,"68b7a1c4-8bc2-4b87-af8e-2383ff06fe30102.MirrorCS"),sQuery(id+"F0.wireOp",EDGE,"68b7a1c4-8bc2-4b87-af8e-2383ff06fe30103.MirrorCS"),sQuery(id+"F0.wireOp",EDGE,"68b7a1c4-8bc2-4b87-af8e-2383ff06fe30104.MirrorCS"),sQuery(id+"F0.wireOp",EDGE,"68b7a1c4-8bc2-4b87-af8e-2383ff06fe30105.MirrorCS"),sQuery(id+"F0.wireOp",EDGE,"68b7a1c4-8bc2-4b87-af8e-2383ff06fe30106.MirrorCS"),sQuery(id+"F0.wireOp",EDGE,"68b7a1c4-8bc2-4b87-af8e-2383ff06fe30107.MirrorCS"),sQuery(id+"F0.wireOp",EDGE,"68b7a1c4-8bc2-4b87-af8e-2383ff06fe30108.MirrorCS"),sQuery(id+"F0.wireOp",EDGE,"68b7a1c4-8bc2-4b87-af8e-2383ff06fe30109.MirrorCS"),sQuery(id+"F0.wireOp",EDGE,"68b7a1c4-8bc2-4b87-af8e-2383ff06fe30111.MirrorCS"),sQuery(id+"F0.wireOp",EDGE,"68b7a1c4-8bc2-4b87-af8e-2383ff06fe30112.MirrorCS"),sQuery(id+"F0.wireOp",EDGE,"68b7a1c4-8bc2-4b87-af8e-2383ff06fe30113.MirrorCS"),sQuery(id+"F0.wireOp",EDGE,"68b7a1c4-8bc2-4b87-af8e-2383ff06fe30114.MirrorCS"),sQuery(id+"F0.wireOp",EDGE,"68b7a1c4-8bc2-4b87-af8e-2383ff06fe30115.MirrorCS"),sQuery(id+"F0.wireOp",EDGE,"68b7a1c4-8bc2-4b87-af8e-2383ff06fe30116.MirrorCS"),sQuery(id+"F0.wireOp",EDGE,"68b7a1c4-8bc2-4b87-af8e-2383ff06fe30117.MirrorCS"),sQuery(id+"F0.wireOp",EDGE,"68b7a1c4-8bc2-4b87-af8e-2383ff06fe30118.MirrorCS"),sQuery(id+"F0.wireOp",EDGE,"68b7a1c4-8bc2-4b87-af8e-2383ff06fe30119.MirrorCS"),sQuery(id+"F0.wireOp",EDGE,"68b7a1c4-8bc2-4b87-af8e-2383ff06fe30120.MirrorCS"),sQuery(id+"F0.wireOp",EDGE,"68b7a1c4-8bc2-4b87-af8e-2383ff06fe30121.MirrorCS"),sQuery(id+"F0.wireOp",EDGE,"68b7a1c4-8bc2-4b87-af8e-2383ff06fe30122.MirrorCS"),sQuery(id+"F0.wireOp",EDGE,"68b7a1c4-8bc2-4b87-af8e-2383ff06fe30123.MirrorCS"),sQuery(id+"F0.wireOp",EDGE,"68b7a1c4-8bc2-4b87-af8e-2383ff06fe30124.MirrorCS"),sQuery(id+"F0.wireOp",EDGE,"68b7a1c4-8bc2-4b87-af8e-2383ff06fe30125.MirrorCS"),sQuery(id+"F0.wireOp",EDGE,"68b7a1c4-8bc2-4b87-af8e-2383ff06fe30126.MirrorCS"),sQuery(id+"F0.wireOp",EDGE,"68b7a1c4-8bc2-4b87-af8e-2383ff06fe30127.MirrorCS"),sQuery(id+"F0.wireOp",EDGE,"68b7a1c4-8bc2-4b87-af8e-2383ff06fe30128.MirrorCS"),sQuery(id+"F0.wireOp",EDGE,"68b7a1c4-8bc2-4b87-af8e-2383ff06fe30129.MirrorCS"),sQuery(id+"F0.wireOp",EDGE,"68b7a1c4-8bc2-4b87-af8e-2383ff06fe30130.MirrorCS"),sQuery(id+"F0.wireOp",EDGE,"68b7a1c4-8bc2-4b87-af8e-2383ff06fe30131.MirrorCS"),sQuery(id+"F0.wireOp",EDGE,"68b7a1c4-8bc2-4b87-af8e-2383ff06fe30132.MirrorCS"),sQuery(id+"F0.wireOp",EDGE,"68b7a1c4-8bc2-4b87-af8e-2383ff06fe30133.MirrorCS"),sQuery(id+"F0.wireOp",EDGE,"68b7a1c4-8bc2-4b87-af8e-2383ff06fe30134.MirrorCS"),sQuery(id+"F0.wireOp",EDGE,"68b7a1c4-8bc2-4b87-af8e-2383ff06fe30135.MirrorCS"),sQuery(id+"F0.wireOp",EDGE,"68b7a1c4-8bc2-4b87-af8e-2383ff06fe30136.MirrorCS"),sQuery(id+"F0.wireOp",EDGE,"68b7a1c4-8bc2-4b87-af8e-2383ff06fe30137.MirrorCS"),sQuery(id+"F0.wireOp",EDGE,"68b7a1c4-8bc2-4b87-af8e-2383ff06fe30138.MirrorCS"),sQuery(id+"F0.wireOp",EDGE,"68b7a1c4-8bc2-4b87-af8e-2383ff06fe30139.MirrorCS"),sQuery(id+"F0.wireOp",EDGE,"68b7a1c4-8bc2-4b87-af8e-2383ff06fe30140.MirrorCS"),sQuery(id+"F0.wireOp",EDGE,"68b7a1c4-8bc2-4b87-af8e-2383ff06fe30141.MirrorCS"),sQuery(id+"F0.wireOp",EDGE,"68b7a1c4-8bc2-4b87-af8e-2383ff06fe30142.MirrorCS"),sQuery(id+"F0.wireOp",EDGE,"68b7a1c4-8bc2-4b87-af8e-2383ff06fe30143.MirrorCS"),sQuery(id+"F0.wireOp",EDGE,"68b7a1c4-8bc2-4b87-af8e-2383ff06fe30145.MirrorCS"),sQuery(id+"F0.wireOp",EDGE,"68b7a1c4-8bc2-4b87-af8e-2383ff06fe30146.MirrorCS"),sQuery(id+"F0.wireOp",EDGE,"68b7a1c4-8bc2-4b87-af8e-2383ff06fe30147.MirrorCS"),sQuery(id+"F0.wireOp",EDGE,"68b7a1c4-8bc2-4b87-af8e-2383ff06fe30148.MirrorCS"),sQuery(id+"F0.wireOp",EDGE,"68b7a1c4-8bc2-4b87-af8e-2383ff06fe30149.MirrorCS"),sQuery(id+"F0.wireOp",EDGE,"68b7a1c4-8bc2-4b87-af8e-2383ff06fe30150.MirrorCS"),sQuery(id+"F0.wireOp",EDGE,"68b7a1c4-8bc2-4b87-af8e-2383ff06fe30151.MirrorCS"),sQuery(id+"F0.wireOp",EDGE,"68b7a1c4-8bc2-4b87-af8e-2383ff06fe30152.MirrorCS"),sQuery(id+"F0.wireOp",EDGE,"68b7a1c4-8bc2-4b87-af8e-2383ff06fe30153.MirrorCS"),sQuery(id+"F0.wireOp",EDGE,"68b7a1c4-8bc2-4b87-af8e-2383ff06fe30154.MirrorCS"),sQuery(id+"F0.wireOp",EDGE,"68b7a1c4-8bc2-4b87-af8e-2383ff06fe30155.MirrorCS"),sQuery(id+"F0.wireOp",EDGE,"68b7a1c4-8bc2-4b87-af8e-2383ff06fe30156.MirrorCS"),sQuery(id+"F0.wireOp",EDGE,"68b7a1c4-8bc2-4b87-af8e-2383ff06fe30157.MirrorCS"),sQuery(id+"F0.wireOp",EDGE,"68b7a1c4-8bc2-4b87-af8e-2383ff06fe30158.MirrorCS"),sQuery(id+"F0.wireOp",EDGE,"68b7a1c4-8bc2-4b87-af8e-2383ff06fe30159.MirrorCS"),sQuery(id+"F0.wireOp",EDGE,"68b7a1c4-8bc2-4b87-af8e-2383ff06fe30160.MirrorCS"),sQuery(id+"F0.wireOp",EDGE,"68b7a1c4-8bc2-4b87-af8e-2383ff06fe30161.MirrorCS"),sQuery(id+"F0.wireOp",EDGE,"68b7a1c4-8bc2-4b87-af8e-2383ff06fe30162.MirrorCS"),sQuery(id+"F0.wireOp",EDGE,"68b7a1c4-8bc2-4b87-af8e-2383ff06fe30163.MirrorCS"),sQuery(id+"F0.wireOp",EDGE,"b9f1c8b0-1812-4977-8847-28bb21a96fe669.MirrorCS"),sQuery(id+"F0.wireOp",EDGE,"b9f1c8b0-1812-4977-8847-28bb21a96fe670.MirrorCS"),sQuery(id+"F0.wireOp",EDGE,"b9f1c8b0-1812-4977-8847-28bb21a96fe671.MirrorCS"),sQuery(id+"F0.wireOp",EDGE,"b9f1c8b0-1812-4977-8847-28bb21a96fe672.MirrorCS"),sQuery(id+"F0.wireOp",EDGE,"b9f1c8b0-1812-4977-8847-28bb21a96fe673.MirrorCS"),sQuery(id+"F0.wireOp",EDGE,"b9f1c8b0-1812-4977-8847-28bb21a96fe674.MirrorCS"),sQuery(id+"F0.wireOp",EDGE,"b9f1c8b0-1812-4977-8847-28bb21a96fe675.MirrorCS"),sQuery(id+"F0.wireOp",EDGE,"b9f1c8b0-1812-4977-8847-28bb21a96fe676.MirrorCS"),sQuery(id+"F0.wireOp",EDGE,"b9f1c8b0-1812-4977-8847-28bb21a96fe677.MirrorCS"),sQuery(id+"F0.wireOp",EDGE,"b9f1c8b0-1812-4977-8847-28bb21a96fe678.MirrorCS"),sQuery(id+"F0.wireOp",EDGE,"b9f1c8b0-1812-4977-8847-28bb21a96fe679.MirrorCS"),sQuery(id+"F0.wireOp",EDGE,"b9f1c8b0-1812-4977-8847-28bb21a96fe681.MirrorCS"),sQuery(id+"F0.wireOp",EDGE,"b9f1c8b0-1812-4977-8847-28bb21a96fe682.MirrorCS"),sQuery(id+"F0.wireOp",EDGE,"b9f1c8b0-1812-4977-8847-28bb21a96fe683.MirrorCS"),sQuery(id+"F0.wireOp",EDGE,"b9f1c8b0-1812-4977-8847-28bb21a96fe684.MirrorCS"),sQuery(id+"F0.wireOp",EDGE,"b9f1c8b0-1812-4977-8847-28bb21a96fe685.MirrorCS"),sQuery(id+"F0.wireOp",EDGE,"b9f1c8b0-1812-4977-8847-28bb21a96fe686.MirrorCS"),sQuery(id+"F0.wireOp",EDGE,"b9f1c8b0-1812-4977-8847-28bb21a96fe688.MirrorCS"),sQuery(id+"F0.wireOp",EDGE,"b9f1c8b0-1812-4977-8847-28bb21a96fe689.MirrorCS"),sQuery(id+"F0.wireOp",EDGE,"b9f1c8b0-1812-4977-8847-28bb21a96fe690.MirrorCS"),sQuery(id+"F0.wireOp",EDGE,"b9f1c8b0-1812-4977-8847-28bb21a96fe691.MirrorCS"),sQuery(id+"F0.wireOp",EDGE,"b9f1c8b0-1812-4977-8847-28bb21a96fe692.MirrorCS"),sQuery(id+"F0.wireOp",EDGE,"b9f1c8b0-1812-4977-8847-28bb21a96fe693.MirrorCS"),sQuery(id+"F0.wireOp",EDGE,"b9f1c8b0-1812-4977-8847-28bb21a96fe694.MirrorCS"),sQuery(id+"F0.wireOp",EDGE,"b9f1c8b0-1812-4977-8847-28bb21a96fe695.MirrorCS"),sQuery(id+"F0.wireOp",EDGE,"b9f1c8b0-1812-4977-8847-28bb21a96fe696.MirrorCS"),sQuery(id+"F0.wireOp",EDGE,"b9f1c8b0-1812-4977-8847-28bb21a96fe697.MirrorCS"),sQuery(id+"F0.wireOp",EDGE,"b9f1c8b0-1812-4977-8847-28bb21a96fe698.MirrorCS"),sQuery(id+"F0.wireOp",EDGE,"b9f1c8b0-1812-4977-8847-28bb21a96fe699.MirrorCS"),sQuery(id+"F0.wireOp",EDGE,"b9f1c8b0-1812-4977-8847-28bb21a96fe6100.MirrorCS"),sQuery(id+"F0.wireOp",EDGE,"b9f1c8b0-1812-4977-8847-28bb21a96fe6101.MirrorCS"),sQuery(id+"F0.wireOp",EDGE,"b9f1c8b0-1812-4977-8847-28bb21a96fe6103.MirrorCS"),sQuery(id+"F0.wireOp",EDGE,"b9f1c8b0-1812-4977-8847-28bb21a96fe6104.MirrorCS"),sQuery(id+"F0.wireOp",EDGE,"b9f1c8b0-1812-4977-8847-28bb21a96fe6105.MirrorCS"),sQuery(id+"F0.wireOp",EDGE,"b9f1c8b0-1812-4977-8847-28bb21a96fe6106.MirrorCS"),sQuery(id+"F0.wireOp",EDGE,"b9f1c8b0-1812-4977-8847-28bb21a96fe6107.MirrorCS"),sQuery(id+"F0.wireOp",EDGE,"b9f1c8b0-1812-4977-8847-28bb21a96fe6108.MirrorCS"),sQuery(id+"F0.wireOp",EDGE,"b9f1c8b0-1812-4977-8847-28bb21a96fe6109.MirrorCS"),sQuery(id+"F0.wireOp",EDGE,"b9f1c8b0-1812-4977-8847-28bb21a96fe6111.MirrorCS"),sQuery(id+"F0.wireOp",EDGE,"b9f1c8b0-1812-4977-8847-28bb21a96fe6112.MirrorCS"),sQuery(id+"F0.wireOp",EDGE,"b9f1c8b0-1812-4977-8847-28bb21a96fe6114.MirrorCS"),sQuery(id+"F0.wireOp",EDGE,"b9f1c8b0-1812-4977-8847-28bb21a96fe6115.MirrorCS"),sQuery(id+"F0.wireOp",EDGE,"b9f1c8b0-1812-4977-8847-28bb21a96fe6116.MirrorCS"),sQuery(id+"F0.wireOp",EDGE,"b9f1c8b0-1812-4977-8847-28bb21a96fe6117.MirrorCS"),sQuery(id+"F0.wireOp",EDGE,"b9f1c8b0-1812-4977-8847-28bb21a96fe6118.MirrorCS"),sQuery(id+"F0.wireOp",EDGE,"b9f1c8b0-1812-4977-8847-28bb21a96fe6119.MirrorCS"),sQuery(id+"F0.wireOp",EDGE,"b9f1c8b0-1812-4977-8847-28bb21a96fe6120.MirrorCS"),sQuery(id+"F0.wireOp",EDGE,"b9f1c8b0-1812-4977-8847-28bb21a96fe6121.MirrorCS"),sQuery(id+"F0.wireOp",EDGE,"b9f1c8b0-1812-4977-8847-28bb21a96fe6122.MirrorCS"),sQuery(id+"F0.wireOp",EDGE,"b9f1c8b0-1812-4977-8847-28bb21a96fe6123.MirrorCS"),sQuery(id+"F0.wireOp",EDGE,"b9f1c8b0-1812-4977-8847-28bb21a96fe6124.MirrorCS"),sQuery(id+"F0.wireOp",EDGE,"b9f1c8b0-1812-4977-8847-28bb21a96fe6125.MirrorCS"),sQuery(id+"F0.wireOp",EDGE,"b9f1c8b0-1812-4977-8847-28bb21a96fe6126.MirrorCS"),sQuery(id+"F0.wireOp",EDGE,"b9f1c8b0-1812-4977-8847-28bb21a96fe6127.MirrorCS"),sQuery(id+"F0.wireOp",EDGE,"b9f1c8b0-1812-4977-8847-28bb21a96fe6128.MirrorCS"),sQuery(id+"F0.wireOp",EDGE,"b9f1c8b0-1812-4977-8847-28bb21a96fe6129.MirrorCS"),sQuery(id+"F0.wireOp",EDGE,"b9f1c8b0-1812-4977-8847-28bb21a96fe6131.MirrorCS"),sQuery(id+"F0.wireOp",EDGE,"b9f1c8b0-1812-4977-8847-28bb21a96fe6132.MirrorCS"),sQuery(id+"F0.wireOp",EDGE,"b9f1c8b0-1812-4977-8847-28bb21a96fe6133.MirrorCS"),sQuery(id+"F0.wireOp",EDGE,"b9f1c8b0-1812-4977-8847-28bb21a96fe6135.MirrorCS"),sQuery(id+"F0.wireOp",EDGE,"b9f1c8b0-1812-4977-8847-28bb21a96fe6136.MirrorCS"),sQuery(id+"F0.wireOp",EDGE,"b9f1c8b0-1812-4977-8847-28bb21a96fe6137.MirrorCS"),sQuery(id+"F0.wireOp",EDGE,"b9f1c8b0-1812-4977-8847-28bb21a96fe6138.MirrorCS"),sQuery(id+"F0.wireOp",EDGE,"b9f1c8b0-1812-4977-8847-28bb21a96fe6140.MirrorCS"),sQuery(id+"F0.wireOp",EDGE,"b9f1c8b0-1812-4977-8847-28bb21a96fe6144.MirrorCS"),sQuery(id+"F0.wireOp",EDGE,"b9f1c8b0-1812-4977-8847-28bb21a96fe6147.MirrorCS"),sQuery(id+"F0.wireOp",EDGE,"b9f1c8b0-1812-4977-8847-28bb21a96fe6179.MirrorCS"),sQuery(id+"F0.wireOp",EDGE,"b9f1c8b0-1812-4977-8847-28bb21a96fe6184.MirrorCS"),sQuery(id+"F0.wireOp",EDGE,"b9f1c8b0-1812-4977-8847-28bb21a96fe6240.MirrorCS"),sQuery(id+"F0.wireOp",EDGE,"b9f1c8b0-1812-4977-8847-28bb21a96fe6241.MirrorCS"),sQuery(id+"F0.wireOp",EDGE,"b9f1c8b0-1812-4977-8847-28bb21a96fe6242.MirrorCS"),sQuery(id+"F0.wireOp",EDGE,"b9f1c8b0-1812-4977-8847-28bb21a96fe6243.MirrorCS"),sQuery(id+"F0.wireOp",EDGE,"b9f1c8b0-1812-4977-8847-28bb21a96fe6244.MirrorCS"),sQuery(id+"F0.wireOp",EDGE,"b9f1c8b0-1812-4977-8847-28bb21a96fe6245.MirrorCS"),sQuery(id+"F0.wireOp",EDGE,"b9f1c8b0-1812-4977-8847-28bb21a96fe6246.MirrorCS"),sQuery(id+"F0.wireOp",EDGE,"b9f1c8b0-1812-4977-8847-28bb21a96fe6247.MirrorCS"),sQuery(id+"F0.wireOp",EDGE,"b9f1c8b0-1812-4977-8847-28bb21a96fe6248.MirrorCS"),sQuery(id+"F0.wireOp",EDGE,"b9f1c8b0-1812-4977-8847-28bb21a96fe6250.MirrorCS"),sQuery(id+"F0.wireOp",EDGE,"b9f1c8b0-1812-4977-8847-28bb21a96fe6251.MirrorCS"),sQuery(id+"F0.wireOp",EDGE,"b9f1c8b0-1812-4977-8847-28bb21a96fe6252.MirrorCS"),sQuery(id+"F0.wireOp",EDGE,"b9f1c8b0-1812-4977-8847-28bb21a96fe6253.MirrorCS"),sQuery(id+"F0.wireOp",EDGE,"b9f1c8b0-1812-4977-8847-28bb21a96fe6254.MirrorCS"),sQuery(id+"F0.wireOp",EDGE,"b9f1c8b0-1812-4977-8847-28bb21a96fe6255.MirrorCS"),sQuery(id+"F0.wireOp",EDGE,"b9f1c8b0-1812-4977-8847-28bb21a96fe6256.MirrorCS"),sQuery(id+"F0.wireOp",EDGE,"b9f1c8b0-1812-4977-8847-28bb21a96fe6257.MirrorCS"),sQuery(id+"F0.wireOp",EDGE,"b9f1c8b0-1812-4977-8847-28bb21a96fe6258.MirrorCS"),sQuery(id+"F0.wireOp",EDGE,"b9f1c8b0-1812-4977-8847-28bb21a96fe6259.MirrorCS"),sQuery(id+"F0.wireOp",EDGE,"b9f1c8b0-1812-4977-8847-28bb21a96fe6260.MirrorCS"),sQuery(id+"F0.wireOp",EDGE,"b9f1c8b0-1812-4977-8847-28bb21a96fe6261.MirrorCS"),sQuery(id+"F0.wireOp",EDGE,"b9f1c8b0-1812-4977-8847-28bb21a96fe6262.MirrorCS"),sQuery(id+"F0.wireOp",EDGE,"b9f1c8b0-1812-4977-8847-28bb21a96fe6263.MirrorCS"),sQuery(id+"F0.wireOp",EDGE,"b9f1c8b0-1812-4977-8847-28bb21a96fe6264.MirrorCS"),sQuery(id+"F0.wireOp",EDGE,"b9f1c8b0-1812-4977-8847-28bb21a96fe6265.MirrorCS"),sQuery(id+"F0.wireOp",EDGE,"b9f1c8b0-1812-4977-8847-28bb21a96fe6266.MirrorCS"),sQuery(id+"F0.wireOp",EDGE,"b9f1c8b0-1812-4977-8847-28bb21a96fe6267.MirrorCS"),sQuery(id+"F0.wireOp",EDGE,"b9f1c8b0-1812-4977-8847-28bb21a96fe6268.MirrorCS"),sQuery(id+"F0.wireOp",EDGE,"b9f1c8b0-1812-4977-8847-28bb21a96fe6269.MirrorCS"),sQuery(id+"F0.wireOp",EDGE,"b9f1c8b0-1812-4977-8847-28bb21a96fe6270.MirrorCS"),sQuery(id+"F0.wireOp",EDGE,"b9f1c8b0-1812-4977-8847-28bb21a96fe6271.MirrorCS"),sQuery(id+"F0.wireOp",EDGE,"b9f1c8b0-1812-4977-8847-28bb21a96fe6272.MirrorCS"),sQuery(id+"F0.wireOp",EDGE,"b9f1c8b0-1812-4977-8847-28bb21a96fe6274.MirrorCS"),sQuery(id+"F0.wireOp",EDGE,"b9f1c8b0-1812-4977-8847-28bb21a96fe6275.MirrorCS"),sQuery(id+"F0.wireOp",EDGE,"b9f1c8b0-1812-4977-8847-28bb21a96fe6276.MirrorCS"),sQuery(id+"F0.wireOp",EDGE,"b9f1c8b0-1812-4977-8847-28bb21a96fe6277.MirrorCS"),sQuery(id+"F0.wireOp",EDGE,"b9f1c8b0-1812-4977-8847-28bb21a96fe6278.MirrorCS"),sQuery(id+"F0.wireOp",EDGE,"b9f1c8b0-1812-4977-8847-28bb21a96fe6279.MirrorCS"),sQuery(id+"F0.wireOp",EDGE,"b9f1c8b0-1812-4977-8847-28bb21a96fe6280.MirrorCS"),sQuery(id+"F0.wireOp",EDGE,"b9f1c8b0-1812-4977-8847-28bb21a96fe6281.MirrorCS"),sQuery(id+"F0.wireOp",EDGE,"b9f1c8b0-1812-4977-8847-28bb21a96fe6282.MirrorCS"),sQuery(id+"F0.wireOp",EDGE,"b9f1c8b0-1812-4977-8847-28bb21a96fe6283.MirrorCS"),sQuery(id+"F0.wireOp",EDGE,"b9f1c8b0-1812-4977-8847-28bb21a96fe6284.MirrorCS"),sQuery(id+"F0.wireOp",EDGE,"b9f1c8b0-1812-4977-8847-28bb21a96fe6286.MirrorCS"),sQuery(id+"F0.wireOp",EDGE,"b9f1c8b0-1812-4977-8847-28bb21a96fe6287.MirrorCS"),sQuery(id+"F0.wireOp",EDGE,"b9f1c8b0-1812-4977-8847-28bb21a96fe6288.MirrorCS"),sQuery(id+"F0.wireOp",EDGE,"b9f1c8b0-1812-4977-8847-28bb21a96fe6289.MirrorCS"),sQuery(id+"F0.wireOp",EDGE,"b9f1c8b0-1812-4977-8847-28bb21a96fe6290.MirrorCS"),sQuery(id+"F0.wireOp",EDGE,"b9f1c8b0-1812-4977-8847-28bb21a96fe6291.MirrorCS"),sQuery(id+"F0.wireOp",EDGE,"b9f1c8b0-1812-4977-8847-28bb21a96fe6292.MirrorCS"),sQuery(id+"F0.wireOp",EDGE,"b9f1c8b0-1812-4977-8847-28bb21a96fe6293.MirrorCS"),sQuery(id+"F0.wireOp",EDGE,"b9f1c8b0-1812-4977-8847-28bb21a96fe6294.MirrorCS"),sQuery(id+"F0.wireOp",EDGE,"b9f1c8b0-1812-4977-8847-28bb21a96fe6295.MirrorCS"),sQuery(id+"F0.wireOp",EDGE,"b9f1c8b0-1812-4977-8847-28bb21a96fe6296.MirrorCS"),sQuery(id+"F0.wireOp",EDGE,"b9f1c8b0-1812-4977-8847-28bb21a96fe6298.MirrorCS"),sQuery(id+"F0.wireOp",EDGE,"b9f1c8b0-1812-4977-8847-28bb21a96fe6299.MirrorCS"),sQuery(id+"F0.wireOp",EDGE,"b9f1c8b0-1812-4977-8847-28bb21a96fe6300.MirrorCS"),sQuery(id+"F0.wireOp",EDGE,"b9f1c8b0-1812-4977-8847-28bb21a96fe6301.MirrorCS"),sQuery(id+"F0.wireOp",EDGE,"b9f1c8b0-1812-4977-8847-28bb21a96fe6302.MirrorCS"),sQuery(id+"F0.wireOp",EDGE,"b9f1c8b0-1812-4977-8847-28bb21a96fe6303.MirrorCS"),sQuery(id+"F0.wireOp",EDGE,"b9f1c8b0-1812-4977-8847-28bb21a96fe6304.MirrorCS"),sQuery(id+"F0.wireOp",EDGE,"b9f1c8b0-1812-4977-8847-28bb21a96fe6305.MirrorCS"),sQuery(id+"F0.wireOp",EDGE,"b9f1c8b0-1812-4977-8847-28bb21a96fe6306.MirrorCS"),sQuery(id+"F0.wireOp",EDGE,"b9f1c8b0-1812-4977-8847-28bb21a96fe6309.MirrorCS"),sQuery(id+"F0.wireOp",EDGE,"b9f1c8b0-1812-4977-8847-28bb21a96fe6310.MirrorCS"),sQuery(id+"F0.wireOp",EDGE,"b9f1c8b0-1812-4977-8847-28bb21a96fe6311.MirrorCS"),sQuery(id+"F0.wireOp",EDGE,"b9f1c8b0-1812-4977-8847-28bb21a96fe6312.MirrorCS"),sQuery(id+"F0.wireOp",EDGE,"b9f1c8b0-1812-4977-8847-28bb21a96fe6313.MirrorCS"),sQuery(id+"F0.wireOp",EDGE,"b9f1c8b0-1812-4977-8847-28bb21a96fe6314.MirrorCS"),sQuery(id+"F0.wireOp",EDGE,"b9f1c8b0-1812-4977-8847-28bb21a96fe6315.MirrorCS"),sQuery(id+"F0.wireOp",EDGE,"b9f1c8b0-1812-4977-8847-28bb21a96fe6316.MirrorCS"),sQuery(id+"F0.wireOp",EDGE,"b9f1c8b0-1812-4977-8847-28bb21a96fe6317.MirrorCS"),sQuery(id+"F0.wireOp",EDGE,"b9f1c8b0-1812-4977-8847-28bb21a96fe6318.MirrorCS"),sQuery(id+"F0.wireOp",EDGE,"b9f1c8b0-1812-4977-8847-28bb21a96fe6319.MirrorCS"),sQuery(id+"F0.wireOp",EDGE,"b9f1c8b0-1812-4977-8847-28bb21a96fe6320.MirrorCS"),sQuery(id+"F0.wireOp",EDGE,"b9f1c8b0-1812-4977-8847-28bb21a96fe6321.MirrorCS"),sQuery(id+"F0.wireOp",EDGE,"b9f1c8b0-1812-4977-8847-28bb21a96fe6322.MirrorCS"),sQuery(id+"F0.wireOp",EDGE,"b9f1c8b0-1812-4977-8847-28bb21a96fe6323.MirrorCS"),sQuery(id+"F0.wireOp",EDGE,"b9f1c8b0-1812-4977-8847-28bb21a96fe6324.MirrorCS"),sQuery(id+"F0.wireOp",EDGE,"b9f1c8b0-1812-4977-8847-28bb21a96fe6326.MirrorCS"),sQuery(id+"F0.wireOp",EDGE,"1b0cb521-1372-4fad-a006-b8d427d7732a4.MirrorCS"),sQuery(id+"F0.wireOp",EDGE,"1b0cb521-1372-4fad-a006-b8d427d7732a5.MirrorCS"),sQuery(id+"F0.wireOp",EDGE,"1b0cb521-1372-4fad-a006-b8d427d7732a6.MirrorCS"),sQuery(id+"F0.wireOp",EDGE,"1b0cb521-1372-4fad-a006-b8d427d7732a7.MirrorCS")])],"isStart":true});
            var sketch = newSketch(context, id + "F7", { "sketchPlane" : qUnion([Q0])});
            skCircle(sketch, "E446", {"center": v(24.5, 33.55) * mm, "radius": 3 * mm});
            skCircle(sketch, "E447", {"center": v(-24.5, 33.55) * mm, "radius": 3 * mm});
            skCircle(sketch, "E448", {"center": v(-24.5, -24.45) * mm, "radius": 3 * mm});
            skCircle(sketch, "E449", {"center": v(24.5, -24.45) * mm, "radius": 3 * mm});
            skCircle(sketch, "E450", {"center": v(20.32, -52.88) * mm, "radius": 1.5 * mm});
            skCircle(sketch, "E451", {"center": v(-20.32, -52.88) * mm, "radius": 1.5 * mm});
            skCircle(sketch, "E452", {"center": v(-20.32, -68.12) * mm, "radius": 1.5 * mm});
            skCircle(sketch, "E453", {"center": v(20.32, -68.12) * mm, "radius": 1.5 * mm});
            skCircle(sketch, "E454", {"center": v(-24.5, -24.45) * mm, "radius": 1.25 * mm});
            skCircle(sketch, "E455", {"center": v(-20.32, -52.88) * mm, "radius": 0.6 * mm});
            skPoint(sketch, "E455.first.point", {"position": v(-20.23, -52.28) * mm});
            skPoint(sketch, "E455.second.point", {"position": v(-20.27, -53.47) * mm});
            skPoint(sketch, "E455.third.point", {"position": v(-20.27, -53.47) * mm});
            skCircle(sketch, "E456", {"center": v(-20.32, -68.12) * mm, "radius": 0.6 * mm});
            skPoint(sketch, "E456.first.point", {"position": v(-20.32, -68.72) * mm});
            skPoint(sketch, "E456.second.point", {"position": v(-19.72, -68.12) * mm});
            skPoint(sketch, "E456.third.point", {"position": v(-20.32, -68.72) * mm});
            skCircle(sketch, "E457", {"center": v(20.32, -52.88) * mm, "radius": 0.6 * mm});
            skPoint(sketch, "E457.first.point", {"position": v(20.42, -53.47) * mm});
            skPoint(sketch, "E457.second.point", {"position": v(20.3, -52.28) * mm});
            skPoint(sketch, "E457.third.point", {"position": v(20.42, -53.47) * mm});
            skCircle(sketch, "E458", {"center": v(20.32, -68.12) * mm, "radius": 0.6 * mm});
            skPoint(sketch, "E458.first.point", {"position": v(20.32, -67.52) * mm});
            skPoint(sketch, "E458.second.point", {"position": v(20.32, -67.52) * mm});
            skPoint(sketch, "E458.third.point", {"position": v(20.23, -67.53) * mm});
            skCircle(sketch, "E459", {"center": v(24.6, -24.45) * mm, "radius": 1.25 * mm});
            skPoint(sketch, "E459.first.point", {"position": v(24.59, -23.2) * mm});
            skPoint(sketch, "E459.second.point", {"position": v(24.52, -25.7) * mm});
            skPoint(sketch, "E459.third.point", {"position": v(24.52, -25.7) * mm});
            skCircle(sketch, "E460", {"center": v(24.5, 33.55) * mm, "radius": 1.25 * mm});
            skPoint(sketch, "E460.first.point", {"position": v(24.53, 32.3) * mm});
            skPoint(sketch, "E460.second.point", {"position": v(24.53, 32.3) * mm});
            skPoint(sketch, "E460.third.point", {"position": v(24.41, 32.3) * mm});
            skCircle(sketch, "E461", {"center": v(-24.51, 36.04) * mm, "radius": 1.25 * mm});
            skPoint(sketch, "E461.first.point", {"position": v(-24.59, 34.8) * mm});
            skPoint(sketch, "E461.second.point", {"position": v(-24.42, 34.8) * mm});
            skPoint(sketch, "E461.third.point", {"position": v(-24.42, 34.8) * mm});
            skSolve(sketch);
        }
        {
            var Q0;
            Q0=makeQuery(id+"F7.imprint","IMPRINT",FACE,{"disambiguationData":[TD([[makeQuery(id+"F7.imprint","IMPRINT",EDGE,{"derivedFrom":sQuery(id+"F7.wireOp",EDGE,"E449")}),1.0]])]});
            var Q1;
            Q1=makeQuery(id+"F7.imprint","IMPRINT",FACE,{"disambiguationData":[TD([[makeQuery(id+"F7.imprint","IMPRINT",EDGE,{"derivedFrom":sQuery(id+"F7.wireOp",EDGE,"E448")}),1.0]])]});
            var Q2;
            Q2=makeQuery(id+"F7.imprint","IMPRINT",FACE,{"disambiguationData":[TD([[makeQuery(id+"F7.imprint","IMPRINT",EDGE,{"derivedFrom":sQuery(id+"F7.wireOp",EDGE,"E446")}),1.0]])]});
            var Q3;
            Q3=makeQuery(id+"F7.imprint","IMPRINT",FACE,{"disambiguationData":[TD([[makeQuery(id+"F7.imprint","IMPRINT",EDGE,{"derivedFrom":sQuery(id+"F7.wireOp",EDGE,"E447")}),1.0]])]});
            extrude(context, id + "F8", {"entities" : qUnion([Q0, Q1, Q2, Q3]), "operationType" : NewBodyOperationType.ADD, "depth" : 3 * mm, "offsetDistance" : 25 * mm});
        }
        {
            var Q0;
            Q0=makeQuery(id+"F7.imprint","IMPRINT",FACE,{"disambiguationData":[TD([[makeQuery(id+"F7.imprint","IMPRINT",EDGE,{"derivedFrom":sQuery(id+"F7.wireOp",EDGE,"E450")}),1.0]])]});
            var Q1;
            Q1=makeQuery(id+"F7.imprint","IMPRINT",FACE,{"disambiguationData":[TD([[makeQuery(id+"F7.imprint","IMPRINT",EDGE,{"derivedFrom":sQuery(id+"F7.wireOp",EDGE,"E453")}),1.0]])]});
            var Q2;
            Q2=makeQuery(id+"F7.imprint","IMPRINT",FACE,{"disambiguationData":[TD([[makeQuery(id+"F7.imprint","IMPRINT",EDGE,{"derivedFrom":sQuery(id+"F7.wireOp",EDGE,"E452")}),1.0]])]});
            var Q3;
            Q3=makeQuery(id+"F7.imprint","IMPRINT",FACE,{"disambiguationData":[TD([[makeQuery(id+"F7.imprint","IMPRINT",EDGE,{"derivedFrom":sQuery(id+"F7.wireOp",EDGE,"E451")}),1.0]])]});
            extrude(context, id + "F9", {"entities" : qUnion([Q0, Q1, Q2, Q3]), "operationType" : NewBodyOperationType.ADD, "oppositeDirection" : true, "depth" : 6 * mm, "offsetDistance" : 25 * mm});
        }
    });
